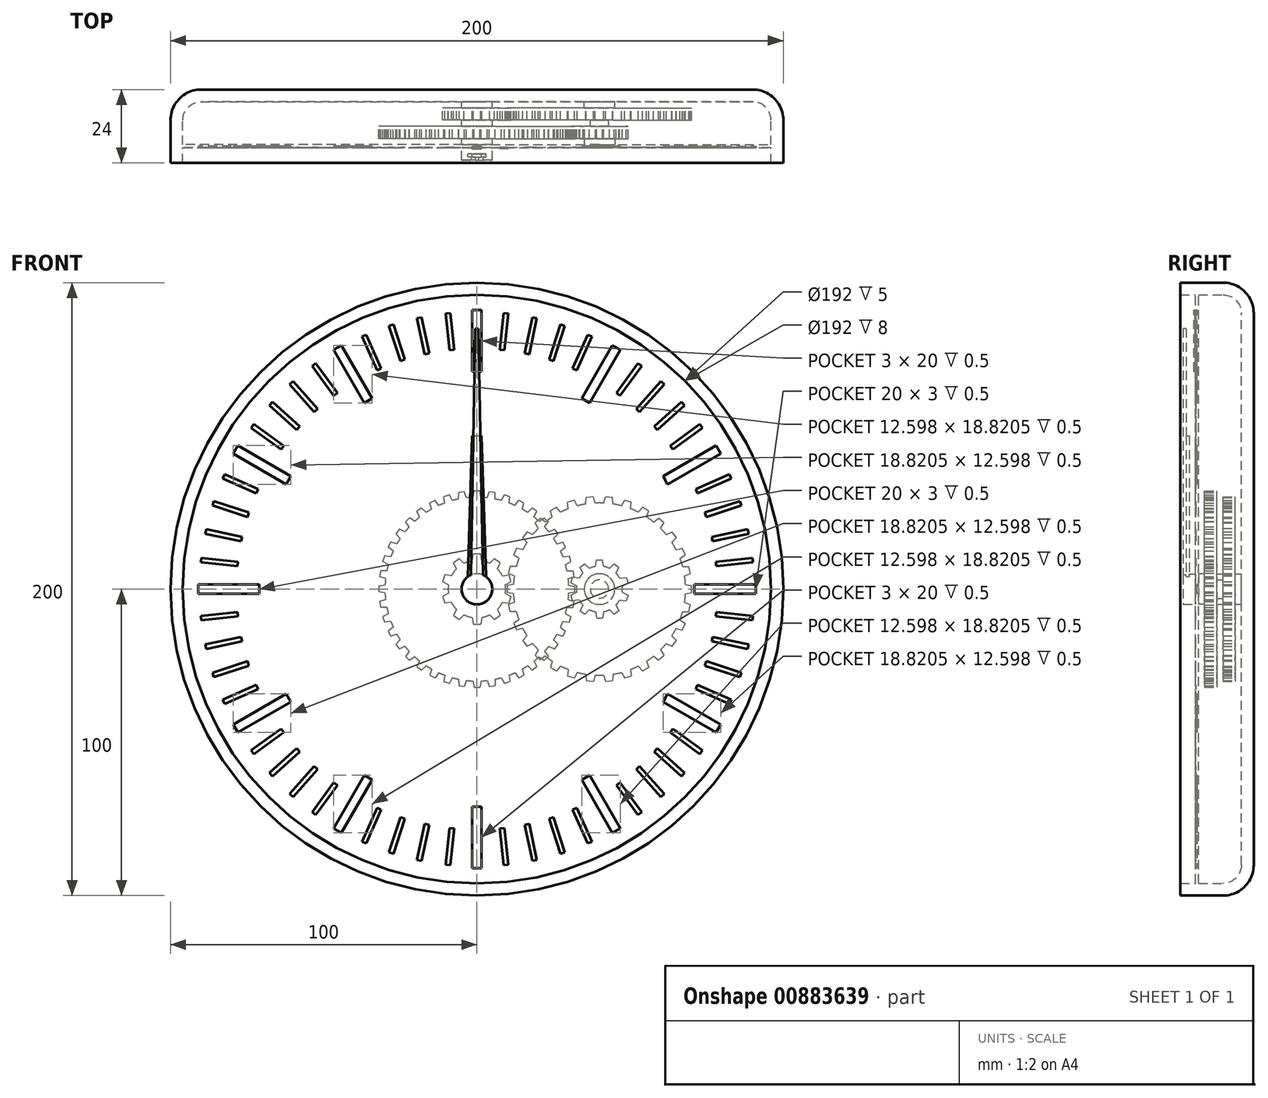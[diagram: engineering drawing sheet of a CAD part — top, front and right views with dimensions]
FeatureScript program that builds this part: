
annotation { "Feature Type Name" : "Feature", "Feature Type Description" : "" }
export const myFeature = defineFeature(function(context is Context, id is Id, definition is map)
    precondition{}
    {
        {
            var Q0;
            Q0=qCreatedBy(makeId("Front.planeOp"),FACE);
            var sketch = newSketch(context, id + "F0", { "sketchPlane" : qUnion([Q0])});
            skCircle(sketch, "E0", {"center": v(0, 0) * mm, "radius": 100 * mm});
            skSolve(sketch);
        }
        {
            var Q0;
            Q0 = qSketchRegion(id + "F0", true);
            extrude(context, id + "F1", {"entities" : qUnion([Q0]), "depth" : 24 * mm, "offsetDistance" : 25 * mm});
        }
        {
            var Q0;
            Q0=makeQuery(id+"F1.opExtrude","CAP_EDGE",EDGE,{"disambiguationData":[OSD([sQuery(id+"F0.wireOp",EDGE,"E0")])],"isStart":true});
            fillet(context, id + "F2", {"entities" : qUnion([Q0]), "radius" : 10 * mm, "tangentPropagation" : true, "allowEdgeOverflow" : false});
        }
        {
            var Q0;
            Q0=makeQuery(id+"F1.opExtrude","CAP_FACE",FACE,{"disambiguationData":[OSD([sQuery(id+"F0.wireOp",EDGE,"E0")])],"isStart":false});
            shell(context, id + "F3", {"entities" : qUnion([Q0]), "thickness" : 4 * mm});
        }
        {
            var Q0;
            {var subQ0=sQuery(id+"F0.wireOp",EDGE,"E0");Q0=makeQuery(id+"F3.opShell","OFFSET_FACE",FACE,{"disambiguationData":[OSD([subQ0]),TDD([makeQuery(id+"F1.opExtrude","CAP_FACE",FACE,{"disambiguationData":[OSD([subQ0])],"isStart":true})])]});}
            var sketch = newSketch(context, id + "F4", { "sketchPlane" : qUnion([Q0])});
            skCircle(sketch, "E1", {"center": v(0, 0) * mm, "radius": 5 * mm});
            skCircle(sketch, "E2", {"center": v(0, 0) * mm, "radius": 3 * mm});
            skCircle(sketch, "E3", {"center": v(40, 0) * mm, "radius": 5 * mm});
            skCircle(sketch, "E4", {"center": v(40, 0) * mm, "radius": 3 * mm});
            skSolve(sketch);
        }
        {
            var Q0;
            Q0 = qSketchRegion(id + "F4", true);
            extrude(context, id + "F5", {"entities" : qUnion([Q0]), "operationType" : NewBodyOperationType.ADD, "depth" : 2 * mm, "offsetDistance" : 25 * mm});
        }
        {
            var Q0;
            {var subQ0=sQuery(id+"F0.wireOp",EDGE,"E0");Q0=makeQuery(id+"F5.boolean.opBoolean","SPLIT",FACE,{"disambiguationData":[TD([makeQuery(id+"F5.opExtrude","SWEPT_FACE",FACE,{"disambiguationData":[OSD([sQuery(id+"F4.wireOp",EDGE,"E2")])]})])],"derivedFrom":makeQuery(id+"F3.opShell","OFFSET_FACE",FACE,{"disambiguationData":[OSD([subQ0]),TDD([makeQuery(id+"F1.opExtrude","CAP_FACE",FACE,{"disambiguationData":[OSD([subQ0])],"isStart":true})])]})});}
            extrude(context, id + "F6", {"entities" : qUnion([Q0]), "depth" : 19 * mm, "offsetDistance" : 25 * mm});
        }
        {
            var Q0;
            {var subQ0=sQuery(id+"F0.wireOp",EDGE,"E0");Q0=makeQuery(id+"F5.boolean.opBoolean","SPLIT",FACE,{"disambiguationData":[TD([makeQuery(id+"F5.opExtrude","SWEPT_FACE",FACE,{"disambiguationData":[OSD([sQuery(id+"F4.wireOp",EDGE,"E4")])]})])],"derivedFrom":makeQuery(id+"F3.opShell","OFFSET_FACE",FACE,{"disambiguationData":[OSD([subQ0]),TDD([makeQuery(id+"F1.opExtrude","CAP_FACE",FACE,{"disambiguationData":[OSD([subQ0])],"isStart":true})])]})});}
            extrude(context, id + "F7", {"entities" : qUnion([Q0]), "depth" : 8 * mm, "offsetDistance" : 25 * mm});
        }
        {
            var Q0;
            Q0=makeQuery(id+"F5.opExtrude","CAP_FACE",FACE,{"disambiguationData":[OSD([sQuery(id+"F4.wireOp",EDGE,"E1"),sQuery(id+"F4.wireOp",EDGE,"E2")])],"isStart":false});
            var sketch = newSketch(context, id + "F8", { "sketchPlane" : qUnion([Q0])});
            skCircle(sketch, "E5", {"center": v(0, 0) * mm, "radius": 9.38 * mm});
            skLineSegment(sketch, "E6", {"start": v(1.55, 9.25) * mm, "end": v(1.18, 11.38) * mm});
            skLineSegment(sketch, "E7", {"start": v(1.18, 11.38) * mm, "end": v(0, 11.38) * mm});
            skLineSegment(sketch, "E8.MirrorCS", {"start": v(-1.18, 11.38) * mm, "end": v(0, 11.38) * mm});
            skLineSegment(sketch, "E9.MirrorCS", {"start": v(-1.55, 9.25) * mm, "end": v(-1.18, 11.38) * mm});
            skLineSegment(sketch, "E10.1.0", {"start": v(-6.7, 6.57) * mm, "end": v(-7.64, 8.51) * mm});
            skLineSegment(sketch, "E10.1.1", {"start": v(-7.64, 8.51) * mm, "end": v(-6.69, 9.2) * mm});
            skLineSegment(sketch, "E10.1.2", {"start": v(-5.73, 9.9) * mm, "end": v(-6.69, 9.2) * mm});
            skLineSegment(sketch, "E10.1.3", {"start": v(-4.18, 8.4) * mm, "end": v(-5.73, 9.9) * mm});
            skLineSegment(sketch, "E10.2.0", {"start": v(-9.27, 1.38) * mm, "end": v(-11.18, 2.4) * mm});
            skLineSegment(sketch, "E10.2.1", {"start": v(-11.18, 2.4) * mm, "end": v(-10.82, 3.52) * mm});
            skLineSegment(sketch, "E10.2.2", {"start": v(-10.45, 4.64) * mm, "end": v(-10.82, 3.52) * mm});
            skLineSegment(sketch, "E10.2.3", {"start": v(-8.31, 4.33) * mm, "end": v(-10.45, 4.64) * mm});
            skLineSegment(sketch, "E11.1.3.0", {"start": v(-8.31, -4.33) * mm, "end": v(-10.45, -4.64) * mm});
            skLineSegment(sketch, "E11.3.3.0", {"start": v(-10.45, -4.64) * mm, "end": v(-10.82, -3.52) * mm});
            skLineSegment(sketch, "E11.6.3.0", {"start": v(-11.18, -2.4) * mm, "end": v(-10.82, -3.52) * mm});
            skLineSegment(sketch, "E11.9.3.0", {"start": v(-9.27, -1.38) * mm, "end": v(-11.18, -2.4) * mm});
            skLineSegment(sketch, "E11.1.4.0", {"start": v(-4.18, -8.4) * mm, "end": v(-5.73, -9.9) * mm});
            skLineSegment(sketch, "E11.3.4.0", {"start": v(-5.73, -9.9) * mm, "end": v(-6.69, -9.2) * mm});
            skLineSegment(sketch, "E11.6.4.0", {"start": v(-7.64, -8.51) * mm, "end": v(-6.69, -9.2) * mm});
            skLineSegment(sketch, "E11.9.4.0", {"start": v(-6.7, -6.57) * mm, "end": v(-7.64, -8.51) * mm});
            skLineSegment(sketch, "E11.1.5.0", {"start": v(1.55, -9.25) * mm, "end": v(1.18, -11.38) * mm});
            skLineSegment(sketch, "E11.3.5.0", {"start": v(1.18, -11.38) * mm, "end": v(0, -11.38) * mm});
            skLineSegment(sketch, "E11.6.5.0", {"start": v(-1.18, -11.38) * mm, "end": v(0, -11.38) * mm});
            skLineSegment(sketch, "E11.9.5.0", {"start": v(-1.55, -9.25) * mm, "end": v(-1.18, -11.38) * mm});
            skLineSegment(sketch, "E11.1.6.0", {"start": v(6.7, -6.57) * mm, "end": v(7.64, -8.51) * mm});
            skLineSegment(sketch, "E11.3.6.0", {"start": v(7.64, -8.51) * mm, "end": v(6.69, -9.2) * mm});
            skLineSegment(sketch, "E11.6.6.0", {"start": v(5.73, -9.9) * mm, "end": v(6.69, -9.2) * mm});
            skLineSegment(sketch, "E11.9.6.0", {"start": v(4.18, -8.4) * mm, "end": v(5.73, -9.9) * mm});
            skLineSegment(sketch, "E11.1.7.0", {"start": v(9.27, -1.38) * mm, "end": v(11.18, -2.4) * mm});
            skLineSegment(sketch, "E11.3.7.0", {"start": v(11.18, -2.4) * mm, "end": v(10.82, -3.52) * mm});
            skLineSegment(sketch, "E11.6.7.0", {"start": v(10.45, -4.64) * mm, "end": v(10.82, -3.52) * mm});
            skLineSegment(sketch, "E11.9.7.0", {"start": v(8.31, -4.33) * mm, "end": v(10.45, -4.64) * mm});
            skLineSegment(sketch, "E11.1.8.0", {"start": v(8.31, 4.33) * mm, "end": v(10.45, 4.64) * mm});
            skLineSegment(sketch, "E11.3.8.0", {"start": v(10.45, 4.64) * mm, "end": v(10.82, 3.52) * mm});
            skLineSegment(sketch, "E11.6.8.0", {"start": v(11.18, 2.4) * mm, "end": v(10.82, 3.52) * mm});
            skLineSegment(sketch, "E11.9.8.0", {"start": v(9.27, 1.38) * mm, "end": v(11.18, 2.4) * mm});
            skLineSegment(sketch, "E11.1.9.0", {"start": v(4.18, 8.4) * mm, "end": v(5.73, 9.9) * mm});
            skLineSegment(sketch, "E11.3.9.0", {"start": v(5.73, 9.9) * mm, "end": v(6.69, 9.2) * mm});
            skLineSegment(sketch, "E11.6.9.0", {"start": v(7.64, 8.51) * mm, "end": v(6.69, 9.2) * mm});
            skLineSegment(sketch, "E11.9.9.0", {"start": v(6.7, 6.57) * mm, "end": v(7.64, 8.51) * mm});
            skSolve(sketch);
        }
        {
            var Q0;
            Q0 = qSketchRegion(id + "F8", true);
            extrude(context, id + "F9", {"entities" : qUnion([Q0]), "operationType" : NewBodyOperationType.ADD, "depth" : 4 * mm, "offsetDistance" : 25 * mm});
        }
        {
            var Q0;
            Q0=makeQuery(id+"F5.opExtrude","CAP_FACE",FACE,{"disambiguationData":[OSD([sQuery(id+"F4.wireOp",EDGE,"E3"),sQuery(id+"F4.wireOp",EDGE,"E4")])],"isStart":false});
            var sketch = newSketch(context, id + "F10", { "sketchPlane" : qUnion([Q0])});
            skCircle(sketch, "E12", {"center": v(40, 0) * mm, "radius": 28.12 * mm});
            skLineSegment(sketch, "E13", {"start": v(11.92, 1.54) * mm, "end": v(9.88, 1.18) * mm});
            skLineSegment(sketch, "E14", {"start": v(9.88, 1.18) * mm, "end": v(9.88, 0) * mm});
            skLineSegment(sketch, "E15.MirrorCS", {"start": v(11.92, -1.54) * mm, "end": v(9.87, -1.18) * mm});
            skLineSegment(sketch, "E16.MirrorCS", {"start": v(9.88, -1.18) * mm, "end": v(9.88, 0) * mm});
            skLineSegment(sketch, "E17.1.0", {"start": v(12.21, -4.33) * mm, "end": v(10.29, -5.11) * mm});
            skLineSegment(sketch, "E17.1.1", {"start": v(10.29, -5.11) * mm, "end": v(10.53, -6.26) * mm});
            skLineSegment(sketch, "E17.1.2", {"start": v(10.78, -7.42) * mm, "end": v(10.53, -6.26) * mm});
            skLineSegment(sketch, "E17.1.3", {"start": v(12.85, -7.34) * mm, "end": v(10.78, -7.42) * mm});
            skLineSegment(sketch, "E17.2.0", {"start": v(13.72, -10.02) * mm, "end": v(12, -11.18) * mm});
            skLineSegment(sketch, "E17.2.1", {"start": v(12, -11.18) * mm, "end": v(12.48, -12.25) * mm});
            skLineSegment(sketch, "E17.2.2", {"start": v(12.96, -13.33) * mm, "end": v(12.48, -12.25) * mm});
            skLineSegment(sketch, "E17.2.3", {"start": v(14.97, -12.83) * mm, "end": v(12.96, -13.33) * mm});
            skLineSegment(sketch, "E18.2.3.0", {"start": v(16.38, -15.26) * mm, "end": v(14.94, -16.75) * mm});
            skLineSegment(sketch, "E18.3.3.0", {"start": v(14.94, -16.75) * mm, "end": v(15.63, -17.7) * mm});
            skLineSegment(sketch, "E18.6.3.0", {"start": v(16.32, -18.66) * mm, "end": v(15.63, -17.7) * mm});
            skLineSegment(sketch, "E18.9.3.0", {"start": v(18.18, -17.75) * mm, "end": v(16.32, -18.66) * mm});
            skLineSegment(sketch, "E18.2.4.0", {"start": v(20.07, -19.84) * mm, "end": v(18.97, -21.6) * mm});
            skLineSegment(sketch, "E18.3.4.0", {"start": v(18.97, -21.6) * mm, "end": v(19.84, -22.39) * mm});
            skLineSegment(sketch, "E18.6.4.0", {"start": v(20.72, -23.18) * mm, "end": v(19.84, -22.39) * mm});
            skLineSegment(sketch, "E18.9.4.0", {"start": v(22.35, -21.9) * mm, "end": v(20.72, -23.18) * mm});
            skLineSegment(sketch, "E18.2.5.0", {"start": v(24.63, -23.55) * mm, "end": v(23.92, -25.5) * mm});
            skLineSegment(sketch, "E18.3.5.0", {"start": v(23.92, -25.5) * mm, "end": v(24.94, -26.09) * mm});
            skLineSegment(sketch, "E18.6.5.0", {"start": v(25.96, -26.68) * mm, "end": v(24.94, -26.09) * mm});
            skLineSegment(sketch, "E18.9.5.0", {"start": v(27.3, -25.09) * mm, "end": v(25.96, -26.68) * mm});
            skLineSegment(sketch, "E18.2.6.0", {"start": v(29.86, -26.23) * mm, "end": v(29.57, -28.29) * mm});
            skLineSegment(sketch, "E18.3.6.0", {"start": v(29.57, -28.29) * mm, "end": v(30.7, -28.65) * mm});
            skLineSegment(sketch, "E18.6.6.0", {"start": v(31.81, -29.01) * mm, "end": v(30.7, -28.65) * mm});
            skLineSegment(sketch, "E18.9.6.0", {"start": v(32.78, -27.18) * mm, "end": v(31.81, -29.01) * mm});
            skLineSegment(sketch, "E18.2.7.0", {"start": v(35.53, -27.77) * mm, "end": v(35.68, -29.84) * mm});
            skLineSegment(sketch, "E18.3.7.0", {"start": v(35.68, -29.84) * mm, "end": v(36.85, -29.96) * mm});
            skLineSegment(sketch, "E18.6.7.0", {"start": v(38.02, -30.08) * mm, "end": v(36.85, -29.96) * mm});
            skLineSegment(sketch, "E18.9.7.0", {"start": v(38.6, -28.09) * mm, "end": v(38.02, -30.08) * mm});
            skLineSegment(sketch, "E18.2.8.0", {"start": v(41.4, -28.09) * mm, "end": v(41.98, -30.08) * mm});
            skLineSegment(sketch, "E18.3.8.0", {"start": v(41.98, -30.08) * mm, "end": v(43.15, -29.96) * mm});
            skLineSegment(sketch, "E18.6.8.0", {"start": v(44.32, -29.84) * mm, "end": v(43.15, -29.96) * mm});
            skLineSegment(sketch, "E18.9.8.0", {"start": v(44.47, -27.77) * mm, "end": v(44.32, -29.84) * mm});
            skLineSegment(sketch, "E18.2.9.0", {"start": v(47.22, -27.18) * mm, "end": v(48.19, -29.01) * mm});
            skLineSegment(sketch, "E18.3.9.0", {"start": v(48.19, -29.01) * mm, "end": v(49.3, -28.65) * mm});
            skLineSegment(sketch, "E18.6.9.0", {"start": v(50.43, -28.29) * mm, "end": v(49.3, -28.65) * mm});
            skLineSegment(sketch, "E18.9.9.0", {"start": v(50.14, -26.23) * mm, "end": v(50.43, -28.29) * mm});
            skLineSegment(sketch, "E18.2.10.0", {"start": v(52.7, -25.09) * mm, "end": v(54.04, -26.68) * mm});
            skLineSegment(sketch, "E18.3.10.0", {"start": v(54.04, -26.68) * mm, "end": v(55.06, -26.09) * mm});
            skLineSegment(sketch, "E18.6.10.0", {"start": v(56.08, -25.5) * mm, "end": v(55.06, -26.09) * mm});
            skLineSegment(sketch, "E18.9.10.0", {"start": v(55.37, -23.55) * mm, "end": v(56.08, -25.5) * mm});
            skLineSegment(sketch, "E18.2.11.0", {"start": v(57.65, -21.9) * mm, "end": v(59.28, -23.18) * mm});
            skLineSegment(sketch, "E18.3.11.0", {"start": v(59.28, -23.18) * mm, "end": v(60.16, -22.39) * mm});
            skLineSegment(sketch, "E18.6.11.0", {"start": v(61.03, -21.6) * mm, "end": v(60.16, -22.39) * mm});
            skLineSegment(sketch, "E18.9.11.0", {"start": v(59.93, -19.84) * mm, "end": v(61.03, -21.6) * mm});
            skLineSegment(sketch, "E18.2.12.0", {"start": v(61.82, -17.75) * mm, "end": v(63.68, -18.66) * mm});
            skLineSegment(sketch, "E18.3.12.0", {"start": v(63.68, -18.66) * mm, "end": v(64.37, -17.7) * mm});
            skLineSegment(sketch, "E18.6.12.0", {"start": v(65.06, -16.75) * mm, "end": v(64.37, -17.7) * mm});
            skLineSegment(sketch, "E18.9.12.0", {"start": v(63.62, -15.26) * mm, "end": v(65.06, -16.75) * mm});
            skLineSegment(sketch, "E18.2.13.0", {"start": v(65.03, -12.83) * mm, "end": v(67.04, -13.33) * mm});
            skLineSegment(sketch, "E18.3.13.0", {"start": v(67.04, -13.33) * mm, "end": v(67.52, -12.25) * mm});
            skLineSegment(sketch, "E18.6.13.0", {"start": v(68, -11.18) * mm, "end": v(67.52, -12.25) * mm});
            skLineSegment(sketch, "E18.9.13.0", {"start": v(66.28, -10.02) * mm, "end": v(68, -11.18) * mm});
            skLineSegment(sketch, "E18.2.14.0", {"start": v(67.15, -7.34) * mm, "end": v(69.22, -7.42) * mm});
            skLineSegment(sketch, "E18.3.14.0", {"start": v(69.22, -7.42) * mm, "end": v(69.47, -6.26) * mm});
            skLineSegment(sketch, "E18.6.14.0", {"start": v(69.71, -5.11) * mm, "end": v(69.47, -6.26) * mm});
            skLineSegment(sketch, "E18.9.14.0", {"start": v(67.79, -4.33) * mm, "end": v(69.71, -5.11) * mm});
            skLineSegment(sketch, "E18.2.15.0", {"start": v(68.08, -1.54) * mm, "end": v(70.12, -1.18) * mm});
            skLineSegment(sketch, "E18.3.15.0", {"start": v(70.12, -1.18) * mm, "end": v(70.12, 0) * mm});
            skLineSegment(sketch, "E18.6.15.0", {"start": v(70.12, 1.18) * mm, "end": v(70.12, 0) * mm});
            skLineSegment(sketch, "E18.9.15.0", {"start": v(68.08, 1.54) * mm, "end": v(70.13, 1.18) * mm});
            skLineSegment(sketch, "E18.2.16.0", {"start": v(67.79, 4.33) * mm, "end": v(69.71, 5.11) * mm});
            skLineSegment(sketch, "E18.3.16.0", {"start": v(69.71, 5.11) * mm, "end": v(69.47, 6.26) * mm});
            skLineSegment(sketch, "E18.6.16.0", {"start": v(69.22, 7.42) * mm, "end": v(69.47, 6.26) * mm});
            skLineSegment(sketch, "E18.9.16.0", {"start": v(67.15, 7.34) * mm, "end": v(69.22, 7.42) * mm});
            skLineSegment(sketch, "E18.2.17.0", {"start": v(66.28, 10.02) * mm, "end": v(68, 11.18) * mm});
            skLineSegment(sketch, "E18.3.17.0", {"start": v(68, 11.18) * mm, "end": v(67.52, 12.25) * mm});
            skLineSegment(sketch, "E18.6.17.0", {"start": v(67.04, 13.33) * mm, "end": v(67.52, 12.25) * mm});
            skLineSegment(sketch, "E18.9.17.0", {"start": v(65.03, 12.83) * mm, "end": v(67.04, 13.33) * mm});
            skLineSegment(sketch, "E18.2.18.0", {"start": v(63.62, 15.26) * mm, "end": v(65.06, 16.75) * mm});
            skLineSegment(sketch, "E18.3.18.0", {"start": v(65.06, 16.75) * mm, "end": v(64.37, 17.7) * mm});
            skLineSegment(sketch, "E18.6.18.0", {"start": v(63.68, 18.66) * mm, "end": v(64.37, 17.7) * mm});
            skLineSegment(sketch, "E18.9.18.0", {"start": v(61.82, 17.75) * mm, "end": v(63.68, 18.66) * mm});
            skLineSegment(sketch, "E18.2.19.0", {"start": v(59.93, 19.84) * mm, "end": v(61.03, 21.6) * mm});
            skLineSegment(sketch, "E18.3.19.0", {"start": v(61.03, 21.6) * mm, "end": v(60.16, 22.39) * mm});
            skLineSegment(sketch, "E18.6.19.0", {"start": v(59.28, 23.18) * mm, "end": v(60.16, 22.39) * mm});
            skLineSegment(sketch, "E18.9.19.0", {"start": v(57.65, 21.9) * mm, "end": v(59.28, 23.18) * mm});
            skLineSegment(sketch, "E18.2.20.0", {"start": v(55.37, 23.55) * mm, "end": v(56.08, 25.5) * mm});
            skLineSegment(sketch, "E18.3.20.0", {"start": v(56.08, 25.5) * mm, "end": v(55.06, 26.09) * mm});
            skLineSegment(sketch, "E18.6.20.0", {"start": v(54.04, 26.68) * mm, "end": v(55.06, 26.09) * mm});
            skLineSegment(sketch, "E18.9.20.0", {"start": v(52.7, 25.09) * mm, "end": v(54.04, 26.68) * mm});
            skLineSegment(sketch, "E18.2.21.0", {"start": v(50.14, 26.23) * mm, "end": v(50.43, 28.29) * mm});
            skLineSegment(sketch, "E18.3.21.0", {"start": v(50.43, 28.29) * mm, "end": v(49.3, 28.65) * mm});
            skLineSegment(sketch, "E18.6.21.0", {"start": v(48.19, 29.01) * mm, "end": v(49.3, 28.65) * mm});
            skLineSegment(sketch, "E18.9.21.0", {"start": v(47.22, 27.18) * mm, "end": v(48.19, 29.01) * mm});
            skLineSegment(sketch, "E18.2.22.0", {"start": v(44.47, 27.77) * mm, "end": v(44.32, 29.84) * mm});
            skLineSegment(sketch, "E18.3.22.0", {"start": v(44.32, 29.84) * mm, "end": v(43.15, 29.96) * mm});
            skLineSegment(sketch, "E18.6.22.0", {"start": v(41.98, 30.08) * mm, "end": v(43.15, 29.96) * mm});
            skLineSegment(sketch, "E18.9.22.0", {"start": v(41.4, 28.09) * mm, "end": v(41.98, 30.08) * mm});
            skLineSegment(sketch, "E18.2.23.0", {"start": v(38.6, 28.09) * mm, "end": v(38.02, 30.08) * mm});
            skLineSegment(sketch, "E18.3.23.0", {"start": v(38.02, 30.08) * mm, "end": v(36.85, 29.96) * mm});
            skLineSegment(sketch, "E18.6.23.0", {"start": v(35.68, 29.84) * mm, "end": v(36.85, 29.96) * mm});
            skLineSegment(sketch, "E18.9.23.0", {"start": v(35.53, 27.77) * mm, "end": v(35.68, 29.84) * mm});
            skLineSegment(sketch, "E18.2.24.0", {"start": v(32.78, 27.18) * mm, "end": v(31.81, 29.01) * mm});
            skLineSegment(sketch, "E18.3.24.0", {"start": v(31.81, 29.01) * mm, "end": v(30.7, 28.65) * mm});
            skLineSegment(sketch, "E18.6.24.0", {"start": v(29.57, 28.29) * mm, "end": v(30.7, 28.65) * mm});
            skLineSegment(sketch, "E18.9.24.0", {"start": v(29.86, 26.23) * mm, "end": v(29.57, 28.29) * mm});
            skLineSegment(sketch, "E18.2.25.0", {"start": v(27.3, 25.09) * mm, "end": v(25.96, 26.68) * mm});
            skLineSegment(sketch, "E18.3.25.0", {"start": v(25.96, 26.68) * mm, "end": v(24.94, 26.09) * mm});
            skLineSegment(sketch, "E18.6.25.0", {"start": v(23.92, 25.5) * mm, "end": v(24.94, 26.09) * mm});
            skLineSegment(sketch, "E18.9.25.0", {"start": v(24.63, 23.55) * mm, "end": v(23.92, 25.5) * mm});
            skLineSegment(sketch, "E18.2.26.0", {"start": v(22.35, 21.9) * mm, "end": v(20.72, 23.18) * mm});
            skLineSegment(sketch, "E18.3.26.0", {"start": v(20.72, 23.18) * mm, "end": v(19.84, 22.39) * mm});
            skLineSegment(sketch, "E18.6.26.0", {"start": v(18.97, 21.6) * mm, "end": v(19.84, 22.39) * mm});
            skLineSegment(sketch, "E18.9.26.0", {"start": v(20.07, 19.84) * mm, "end": v(18.97, 21.6) * mm});
            skLineSegment(sketch, "E18.2.27.0", {"start": v(18.18, 17.75) * mm, "end": v(16.32, 18.66) * mm});
            skLineSegment(sketch, "E18.3.27.0", {"start": v(16.32, 18.66) * mm, "end": v(15.63, 17.7) * mm});
            skLineSegment(sketch, "E18.6.27.0", {"start": v(14.94, 16.75) * mm, "end": v(15.63, 17.7) * mm});
            skLineSegment(sketch, "E18.9.27.0", {"start": v(16.38, 15.26) * mm, "end": v(14.94, 16.75) * mm});
            skLineSegment(sketch, "E18.2.28.0", {"start": v(14.97, 12.83) * mm, "end": v(12.96, 13.33) * mm});
            skLineSegment(sketch, "E18.3.28.0", {"start": v(12.96, 13.33) * mm, "end": v(12.48, 12.25) * mm});
            skLineSegment(sketch, "E18.6.28.0", {"start": v(12, 11.18) * mm, "end": v(12.48, 12.25) * mm});
            skLineSegment(sketch, "E18.9.28.0", {"start": v(13.72, 10.02) * mm, "end": v(12, 11.18) * mm});
            skLineSegment(sketch, "E18.2.29.0", {"start": v(12.85, 7.34) * mm, "end": v(10.78, 7.42) * mm});
            skLineSegment(sketch, "E18.3.29.0", {"start": v(10.78, 7.42) * mm, "end": v(10.53, 6.26) * mm});
            skLineSegment(sketch, "E18.6.29.0", {"start": v(10.29, 5.11) * mm, "end": v(10.53, 6.26) * mm});
            skLineSegment(sketch, "E18.9.29.0", {"start": v(12.21, 4.33) * mm, "end": v(10.29, 5.11) * mm});
            skSolve(sketch);
        }
        {
            var Q0;
            Q0 = qSketchRegion(id + "F10", true);
            extrude(context, id + "F11", {"entities" : qUnion([Q0]), "operationType" : NewBodyOperationType.ADD, "depth" : 4 * mm, "offsetDistance" : 25 * mm});
        }
        {
            var Q0;
            Q0=makeQuery(id+"F9.opExtrude","CAP_FACE",FACE,{"disambiguationData":[OSD([sQuery(id+"F8.wireOp",EDGE,"E5"),sQuery(id+"F8.wireOp",EDGE,"E6"),sQuery(id+"F8.wireOp",EDGE,"E7"),sQuery(id+"F8.wireOp",EDGE,"E8.MirrorCS"),sQuery(id+"F8.wireOp",EDGE,"E9.MirrorCS"),sQuery(id+"F8.wireOp",EDGE,"E10.1.0"),sQuery(id+"F8.wireOp",EDGE,"E10.1.1"),sQuery(id+"F8.wireOp",EDGE,"E10.1.2"),sQuery(id+"F8.wireOp",EDGE,"E10.1.3"),sQuery(id+"F8.wireOp",EDGE,"E10.2.0"),sQuery(id+"F8.wireOp",EDGE,"E10.2.1"),sQuery(id+"F8.wireOp",EDGE,"E10.2.2"),sQuery(id+"F8.wireOp",EDGE,"E10.2.3"),sQuery(id+"F8.wireOp",EDGE,"E11.1.3.0"),sQuery(id+"F8.wireOp",EDGE,"E11.3.3.0"),sQuery(id+"F8.wireOp",EDGE,"E11.6.3.0"),sQuery(id+"F8.wireOp",EDGE,"E11.9.3.0"),sQuery(id+"F8.wireOp",EDGE,"E11.1.4.0"),sQuery(id+"F8.wireOp",EDGE,"E11.3.4.0"),sQuery(id+"F8.wireOp",EDGE,"E11.6.4.0"),sQuery(id+"F8.wireOp",EDGE,"E11.9.4.0"),sQuery(id+"F8.wireOp",EDGE,"E11.1.5.0"),sQuery(id+"F8.wireOp",EDGE,"E11.3.5.0"),sQuery(id+"F8.wireOp",EDGE,"E11.6.5.0"),sQuery(id+"F8.wireOp",EDGE,"E11.9.5.0"),sQuery(id+"F8.wireOp",EDGE,"E11.1.6.0"),sQuery(id+"F8.wireOp",EDGE,"E11.3.6.0"),sQuery(id+"F8.wireOp",EDGE,"E11.6.6.0"),sQuery(id+"F8.wireOp",EDGE,"E11.9.6.0"),sQuery(id+"F8.wireOp",EDGE,"E11.1.7.0"),sQuery(id+"F8.wireOp",EDGE,"E11.3.7.0"),sQuery(id+"F8.wireOp",EDGE,"E11.6.7.0"),sQuery(id+"F8.wireOp",EDGE,"E11.9.7.0"),sQuery(id+"F8.wireOp",EDGE,"E11.1.8.0"),sQuery(id+"F8.wireOp",EDGE,"E11.3.8.0"),sQuery(id+"F8.wireOp",EDGE,"E11.6.8.0"),sQuery(id+"F8.wireOp",EDGE,"E11.9.8.0"),sQuery(id+"F8.wireOp",EDGE,"E11.1.9.0"),sQuery(id+"F8.wireOp",EDGE,"E11.3.9.0"),sQuery(id+"F8.wireOp",EDGE,"E11.6.9.0"),sQuery(id+"F8.wireOp",EDGE,"E11.9.9.0")])],"isStart":false});
            var sketch = newSketch(context, id + "F12", { "sketchPlane" : qUnion([Q0])});
            skCircle(sketch, "E19.0", {"center": v(0, 0) * mm, "radius": 3 * mm});
            skCircle(sketch, "E20.0", {"center": v(0, 0) * mm, "radius": 5 * mm});
            skSolve(sketch);
        }
        {
            var Q0;
            Q0 = qSketchRegion(id + "F12", true);
            extrude(context, id + "F13", {"entities" : qUnion([Q0]), "depth" : 2 * mm, "offsetDistance" : 25 * mm});
        }
        {
            var Q0;
            Q0=makeQuery(id+"F13.opExtrude","CAP_FACE",FACE,{"disambiguationData":[OSD([sQuery(id+"F12.wireOp",EDGE,"E19.0"),sQuery(id+"F12.wireOp",EDGE,"E20.0")])],"isStart":false});
            var sketch = newSketch(context, id + "F14", { "sketchPlane" : qUnion([Q0])});
            skCircle(sketch, "E21.0", {"center": v(0, 0) * mm, "radius": 3 * mm});
            skCircle(sketch, "E22", {"center": v(0, 0) * mm, "radius": 30 * mm});
            skLineSegment(sketch, "E23", {"start": v(1.3, 29.97) * mm, "end": v(0.94, 32) * mm});
            skLineSegment(sketch, "E24", {"start": v(0.94, 32) * mm, "end": v(0, 32) * mm});
            skLineSegment(sketch, "E25.MirrorCS", {"start": v(-1.3, 29.97) * mm, "end": v(-0.94, 32) * mm});
            skLineSegment(sketch, "E26.MirrorCS", {"start": v(-0.94, 32) * mm, "end": v(0, 32) * mm});
            skLineSegment(sketch, "E27.1.0", {"start": v(-3.4, 29.8) * mm, "end": v(-4.08, 31.75) * mm});
            skLineSegment(sketch, "E27.1.1", {"start": v(-4.08, 31.75) * mm, "end": v(-5, 31.6) * mm});
            skLineSegment(sketch, "E27.1.2", {"start": v(-5.94, 31.46) * mm, "end": v(-5, 31.6) * mm});
            skLineSegment(sketch, "E27.1.3", {"start": v(-5.97, 29.4) * mm, "end": v(-5.94, 31.46) * mm});
            skLineSegment(sketch, "E27.2.0", {"start": v(-8.03, 28.9) * mm, "end": v(-9, 30.73) * mm});
            skLineSegment(sketch, "E27.2.1", {"start": v(-9, 30.73) * mm, "end": v(-9.89, 30.43) * mm});
            skLineSegment(sketch, "E27.2.2", {"start": v(-10.78, 30.14) * mm, "end": v(-9.89, 30.43) * mm});
            skLineSegment(sketch, "E27.2.3", {"start": v(-10.5, 28.1) * mm, "end": v(-10.78, 30.14) * mm});
            skLineSegment(sketch, "E28.1.3.0", {"start": v(-12.45, 27.3) * mm, "end": v(-13.69, 28.94) * mm});
            skLineSegment(sketch, "E28.3.3.0", {"start": v(-13.69, 28.94) * mm, "end": v(-14.53, 28.51) * mm});
            skLineSegment(sketch, "E28.6.3.0", {"start": v(-15.37, 28.08) * mm, "end": v(-14.53, 28.51) * mm});
            skLineSegment(sketch, "E28.9.3.0", {"start": v(-14.77, 26.11) * mm, "end": v(-15.37, 28.08) * mm});
            skLineSegment(sketch, "E28.1.4.0", {"start": v(-16.57, 25.01) * mm, "end": v(-18.05, 26.44) * mm});
            skLineSegment(sketch, "E28.3.4.0", {"start": v(-18.05, 26.44) * mm, "end": v(-18.8, 25.89) * mm});
            skLineSegment(sketch, "E28.6.4.0", {"start": v(-19.57, 25.33) * mm, "end": v(-18.8, 25.89) * mm});
            skLineSegment(sketch, "E28.9.4.0", {"start": v(-18.67, 23.48) * mm, "end": v(-19.57, 25.33) * mm});
            skLineSegment(sketch, "E28.1.5.0", {"start": v(-20.27, 22.11) * mm, "end": v(-21.96, 23.3) * mm});
            skLineSegment(sketch, "E28.3.5.0", {"start": v(-21.96, 23.3) * mm, "end": v(-22.63, 22.63) * mm});
            skLineSegment(sketch, "E28.6.5.0", {"start": v(-23.3, 21.96) * mm, "end": v(-22.63, 22.63) * mm});
            skLineSegment(sketch, "E28.9.5.0", {"start": v(-22.11, 20.27) * mm, "end": v(-23.3, 21.96) * mm});
            skLineSegment(sketch, "E28.1.6.0", {"start": v(-23.48, 18.67) * mm, "end": v(-25.33, 19.57) * mm});
            skLineSegment(sketch, "E28.3.6.0", {"start": v(-25.33, 19.57) * mm, "end": v(-25.89, 18.8) * mm});
            skLineSegment(sketch, "E28.6.6.0", {"start": v(-26.44, 18.05) * mm, "end": v(-25.89, 18.8) * mm});
            skLineSegment(sketch, "E28.9.6.0", {"start": v(-25.01, 16.57) * mm, "end": v(-26.44, 18.05) * mm});
            skLineSegment(sketch, "E28.1.7.0", {"start": v(-26.11, 14.77) * mm, "end": v(-28.08, 15.37) * mm});
            skLineSegment(sketch, "E28.3.7.0", {"start": v(-28.08, 15.37) * mm, "end": v(-28.51, 14.53) * mm});
            skLineSegment(sketch, "E28.6.7.0", {"start": v(-28.94, 13.69) * mm, "end": v(-28.51, 14.53) * mm});
            skLineSegment(sketch, "E28.9.7.0", {"start": v(-27.3, 12.45) * mm, "end": v(-28.94, 13.69) * mm});
            skLineSegment(sketch, "E28.1.8.0", {"start": v(-28.1, 10.5) * mm, "end": v(-30.14, 10.78) * mm});
            skLineSegment(sketch, "E28.3.8.0", {"start": v(-30.14, 10.78) * mm, "end": v(-30.43, 9.89) * mm});
            skLineSegment(sketch, "E28.6.8.0", {"start": v(-30.73, 9) * mm, "end": v(-30.43, 9.89) * mm});
            skLineSegment(sketch, "E28.9.8.0", {"start": v(-28.9, 8.03) * mm, "end": v(-30.73, 9) * mm});
            skLineSegment(sketch, "E28.1.9.0", {"start": v(-29.4, 5.97) * mm, "end": v(-31.46, 5.94) * mm});
            skLineSegment(sketch, "E28.3.9.0", {"start": v(-31.46, 5.94) * mm, "end": v(-31.6, 5) * mm});
            skLineSegment(sketch, "E28.6.9.0", {"start": v(-31.75, 4.08) * mm, "end": v(-31.6, 5) * mm});
            skLineSegment(sketch, "E28.9.9.0", {"start": v(-29.8, 3.4) * mm, "end": v(-31.75, 4.08) * mm});
            skLineSegment(sketch, "E28.1.10.0", {"start": v(-29.97, 1.3) * mm, "end": v(-32, 0.94) * mm});
            skLineSegment(sketch, "E28.3.10.0", {"start": v(-32, 0.94) * mm, "end": v(-32, 0) * mm});
            skLineSegment(sketch, "E28.6.10.0", {"start": v(-32, -0.94) * mm, "end": v(-32, 0) * mm});
            skLineSegment(sketch, "E28.9.10.0", {"start": v(-29.97, -1.3) * mm, "end": v(-32, -0.94) * mm});
            skLineSegment(sketch, "E28.1.11.0", {"start": v(-29.8, -3.4) * mm, "end": v(-31.75, -4.08) * mm});
            skLineSegment(sketch, "E28.3.11.0", {"start": v(-31.75, -4.08) * mm, "end": v(-31.6, -5) * mm});
            skLineSegment(sketch, "E28.6.11.0", {"start": v(-31.46, -5.94) * mm, "end": v(-31.6, -5) * mm});
            skLineSegment(sketch, "E28.9.11.0", {"start": v(-29.4, -5.97) * mm, "end": v(-31.46, -5.94) * mm});
            skLineSegment(sketch, "E28.1.12.0", {"start": v(-28.9, -8.03) * mm, "end": v(-30.73, -9) * mm});
            skLineSegment(sketch, "E28.3.12.0", {"start": v(-30.73, -9) * mm, "end": v(-30.43, -9.89) * mm});
            skLineSegment(sketch, "E28.6.12.0", {"start": v(-30.14, -10.78) * mm, "end": v(-30.43, -9.89) * mm});
            skLineSegment(sketch, "E28.9.12.0", {"start": v(-28.1, -10.5) * mm, "end": v(-30.14, -10.78) * mm});
            skLineSegment(sketch, "E28.1.13.0", {"start": v(-27.3, -12.45) * mm, "end": v(-28.94, -13.69) * mm});
            skLineSegment(sketch, "E28.3.13.0", {"start": v(-28.94, -13.69) * mm, "end": v(-28.51, -14.53) * mm});
            skLineSegment(sketch, "E28.6.13.0", {"start": v(-28.08, -15.37) * mm, "end": v(-28.51, -14.53) * mm});
            skLineSegment(sketch, "E28.9.13.0", {"start": v(-26.11, -14.77) * mm, "end": v(-28.08, -15.37) * mm});
            skLineSegment(sketch, "E28.1.14.0", {"start": v(-25.01, -16.57) * mm, "end": v(-26.44, -18.05) * mm});
            skLineSegment(sketch, "E28.3.14.0", {"start": v(-26.44, -18.05) * mm, "end": v(-25.89, -18.8) * mm});
            skLineSegment(sketch, "E28.6.14.0", {"start": v(-25.33, -19.57) * mm, "end": v(-25.89, -18.8) * mm});
            skLineSegment(sketch, "E28.9.14.0", {"start": v(-23.48, -18.67) * mm, "end": v(-25.33, -19.57) * mm});
            skLineSegment(sketch, "E28.1.15.0", {"start": v(-22.11, -20.27) * mm, "end": v(-23.3, -21.96) * mm});
            skLineSegment(sketch, "E28.3.15.0", {"start": v(-23.3, -21.96) * mm, "end": v(-22.63, -22.63) * mm});
            skLineSegment(sketch, "E28.6.15.0", {"start": v(-21.96, -23.3) * mm, "end": v(-22.63, -22.63) * mm});
            skLineSegment(sketch, "E28.9.15.0", {"start": v(-20.27, -22.11) * mm, "end": v(-21.96, -23.3) * mm});
            skLineSegment(sketch, "E28.1.16.0", {"start": v(-18.67, -23.48) * mm, "end": v(-19.57, -25.33) * mm});
            skLineSegment(sketch, "E28.3.16.0", {"start": v(-19.57, -25.33) * mm, "end": v(-18.8, -25.89) * mm});
            skLineSegment(sketch, "E28.6.16.0", {"start": v(-18.05, -26.44) * mm, "end": v(-18.8, -25.89) * mm});
            skLineSegment(sketch, "E28.9.16.0", {"start": v(-16.57, -25.01) * mm, "end": v(-18.05, -26.44) * mm});
            skLineSegment(sketch, "E28.1.17.0", {"start": v(-14.77, -26.11) * mm, "end": v(-15.37, -28.08) * mm});
            skLineSegment(sketch, "E28.3.17.0", {"start": v(-15.37, -28.08) * mm, "end": v(-14.53, -28.51) * mm});
            skLineSegment(sketch, "E28.6.17.0", {"start": v(-13.69, -28.94) * mm, "end": v(-14.53, -28.51) * mm});
            skLineSegment(sketch, "E28.9.17.0", {"start": v(-12.45, -27.3) * mm, "end": v(-13.69, -28.94) * mm});
            skLineSegment(sketch, "E28.1.18.0", {"start": v(-10.5, -28.1) * mm, "end": v(-10.78, -30.14) * mm});
            skLineSegment(sketch, "E28.3.18.0", {"start": v(-10.78, -30.14) * mm, "end": v(-9.89, -30.43) * mm});
            skLineSegment(sketch, "E28.6.18.0", {"start": v(-9, -30.73) * mm, "end": v(-9.89, -30.43) * mm});
            skLineSegment(sketch, "E28.9.18.0", {"start": v(-8.03, -28.9) * mm, "end": v(-9, -30.73) * mm});
            skLineSegment(sketch, "E28.1.19.0", {"start": v(-5.97, -29.4) * mm, "end": v(-5.94, -31.46) * mm});
            skLineSegment(sketch, "E28.3.19.0", {"start": v(-5.94, -31.46) * mm, "end": v(-5, -31.6) * mm});
            skLineSegment(sketch, "E28.6.19.0", {"start": v(-4.08, -31.75) * mm, "end": v(-5, -31.6) * mm});
            skLineSegment(sketch, "E28.9.19.0", {"start": v(-3.4, -29.8) * mm, "end": v(-4.08, -31.75) * mm});
            skLineSegment(sketch, "E28.1.20.0", {"start": v(-1.3, -29.97) * mm, "end": v(-0.94, -32) * mm});
            skLineSegment(sketch, "E28.3.20.0", {"start": v(-0.94, -32) * mm, "end": v(0, -32) * mm});
            skLineSegment(sketch, "E28.6.20.0", {"start": v(0.94, -32) * mm, "end": v(0, -32) * mm});
            skLineSegment(sketch, "E28.9.20.0", {"start": v(1.3, -29.97) * mm, "end": v(0.94, -32) * mm});
            skLineSegment(sketch, "E28.1.21.0", {"start": v(3.4, -29.8) * mm, "end": v(4.08, -31.75) * mm});
            skLineSegment(sketch, "E28.3.21.0", {"start": v(4.08, -31.75) * mm, "end": v(5, -31.6) * mm});
            skLineSegment(sketch, "E28.6.21.0", {"start": v(5.94, -31.46) * mm, "end": v(5, -31.6) * mm});
            skLineSegment(sketch, "E28.9.21.0", {"start": v(5.97, -29.4) * mm, "end": v(5.94, -31.46) * mm});
            skLineSegment(sketch, "E28.1.22.0", {"start": v(8.03, -28.9) * mm, "end": v(9, -30.73) * mm});
            skLineSegment(sketch, "E28.3.22.0", {"start": v(9, -30.73) * mm, "end": v(9.89, -30.43) * mm});
            skLineSegment(sketch, "E28.6.22.0", {"start": v(10.78, -30.14) * mm, "end": v(9.89, -30.43) * mm});
            skLineSegment(sketch, "E28.9.22.0", {"start": v(10.5, -28.1) * mm, "end": v(10.78, -30.14) * mm});
            skLineSegment(sketch, "E28.1.23.0", {"start": v(12.45, -27.3) * mm, "end": v(13.69, -28.94) * mm});
            skLineSegment(sketch, "E28.3.23.0", {"start": v(13.69, -28.94) * mm, "end": v(14.53, -28.51) * mm});
            skLineSegment(sketch, "E28.6.23.0", {"start": v(15.37, -28.08) * mm, "end": v(14.53, -28.51) * mm});
            skLineSegment(sketch, "E28.9.23.0", {"start": v(14.77, -26.11) * mm, "end": v(15.37, -28.08) * mm});
            skLineSegment(sketch, "E28.1.24.0", {"start": v(16.57, -25.01) * mm, "end": v(18.05, -26.44) * mm});
            skLineSegment(sketch, "E28.3.24.0", {"start": v(18.05, -26.44) * mm, "end": v(18.8, -25.89) * mm});
            skLineSegment(sketch, "E28.6.24.0", {"start": v(19.57, -25.33) * mm, "end": v(18.8, -25.89) * mm});
            skLineSegment(sketch, "E28.9.24.0", {"start": v(18.67, -23.48) * mm, "end": v(19.57, -25.33) * mm});
            skLineSegment(sketch, "E28.1.25.0", {"start": v(20.27, -22.11) * mm, "end": v(21.96, -23.3) * mm});
            skLineSegment(sketch, "E28.3.25.0", {"start": v(21.96, -23.3) * mm, "end": v(22.63, -22.63) * mm});
            skLineSegment(sketch, "E28.6.25.0", {"start": v(23.3, -21.96) * mm, "end": v(22.63, -22.63) * mm});
            skLineSegment(sketch, "E28.9.25.0", {"start": v(22.11, -20.27) * mm, "end": v(23.3, -21.96) * mm});
            skLineSegment(sketch, "E28.1.26.0", {"start": v(23.48, -18.67) * mm, "end": v(25.33, -19.57) * mm});
            skLineSegment(sketch, "E28.3.26.0", {"start": v(25.33, -19.57) * mm, "end": v(25.89, -18.8) * mm});
            skLineSegment(sketch, "E28.6.26.0", {"start": v(26.44, -18.05) * mm, "end": v(25.89, -18.8) * mm});
            skLineSegment(sketch, "E28.9.26.0", {"start": v(25.01, -16.57) * mm, "end": v(26.44, -18.05) * mm});
            skLineSegment(sketch, "E28.1.27.0", {"start": v(26.11, -14.77) * mm, "end": v(28.08, -15.37) * mm});
            skLineSegment(sketch, "E28.3.27.0", {"start": v(28.08, -15.37) * mm, "end": v(28.51, -14.53) * mm});
            skLineSegment(sketch, "E28.6.27.0", {"start": v(28.94, -13.69) * mm, "end": v(28.51, -14.53) * mm});
            skLineSegment(sketch, "E28.9.27.0", {"start": v(27.3, -12.45) * mm, "end": v(28.94, -13.69) * mm});
            skLineSegment(sketch, "E28.1.28.0", {"start": v(28.1, -10.5) * mm, "end": v(30.14, -10.78) * mm});
            skLineSegment(sketch, "E28.3.28.0", {"start": v(30.14, -10.78) * mm, "end": v(30.43, -9.89) * mm});
            skLineSegment(sketch, "E28.6.28.0", {"start": v(30.73, -9) * mm, "end": v(30.43, -9.89) * mm});
            skLineSegment(sketch, "E28.9.28.0", {"start": v(28.9, -8.03) * mm, "end": v(30.73, -9) * mm});
            skLineSegment(sketch, "E28.1.29.0", {"start": v(29.4, -5.97) * mm, "end": v(31.46, -5.94) * mm});
            skLineSegment(sketch, "E28.3.29.0", {"start": v(31.46, -5.94) * mm, "end": v(31.6, -5) * mm});
            skLineSegment(sketch, "E28.6.29.0", {"start": v(31.75, -4.08) * mm, "end": v(31.6, -5) * mm});
            skLineSegment(sketch, "E28.9.29.0", {"start": v(29.8, -3.4) * mm, "end": v(31.75, -4.08) * mm});
            skLineSegment(sketch, "E28.1.30.0", {"start": v(29.97, -1.3) * mm, "end": v(32, -0.94) * mm});
            skLineSegment(sketch, "E28.3.30.0", {"start": v(32, -0.94) * mm, "end": v(32, 0) * mm});
            skLineSegment(sketch, "E28.6.30.0", {"start": v(32, 0.94) * mm, "end": v(32, 0) * mm});
            skLineSegment(sketch, "E28.9.30.0", {"start": v(29.97, 1.3) * mm, "end": v(32, 0.94) * mm});
            skLineSegment(sketch, "E28.1.31.0", {"start": v(29.8, 3.4) * mm, "end": v(31.75, 4.08) * mm});
            skLineSegment(sketch, "E28.3.31.0", {"start": v(31.75, 4.08) * mm, "end": v(31.6, 5) * mm});
            skLineSegment(sketch, "E28.6.31.0", {"start": v(31.46, 5.94) * mm, "end": v(31.6, 5) * mm});
            skLineSegment(sketch, "E28.9.31.0", {"start": v(29.4, 5.97) * mm, "end": v(31.46, 5.94) * mm});
            skLineSegment(sketch, "E28.1.32.0", {"start": v(28.9, 8.03) * mm, "end": v(30.73, 9) * mm});
            skLineSegment(sketch, "E28.3.32.0", {"start": v(30.73, 9) * mm, "end": v(30.43, 9.89) * mm});
            skLineSegment(sketch, "E28.6.32.0", {"start": v(30.14, 10.78) * mm, "end": v(30.43, 9.89) * mm});
            skLineSegment(sketch, "E28.9.32.0", {"start": v(28.1, 10.5) * mm, "end": v(30.14, 10.78) * mm});
            skLineSegment(sketch, "E28.1.33.0", {"start": v(27.3, 12.45) * mm, "end": v(28.94, 13.69) * mm});
            skLineSegment(sketch, "E28.3.33.0", {"start": v(28.94, 13.69) * mm, "end": v(28.51, 14.53) * mm});
            skLineSegment(sketch, "E28.6.33.0", {"start": v(28.08, 15.37) * mm, "end": v(28.51, 14.53) * mm});
            skLineSegment(sketch, "E28.9.33.0", {"start": v(26.11, 14.77) * mm, "end": v(28.08, 15.37) * mm});
            skLineSegment(sketch, "E28.1.34.0", {"start": v(25.01, 16.57) * mm, "end": v(26.44, 18.05) * mm});
            skLineSegment(sketch, "E28.3.34.0", {"start": v(26.44, 18.05) * mm, "end": v(25.89, 18.8) * mm});
            skLineSegment(sketch, "E28.6.34.0", {"start": v(25.33, 19.57) * mm, "end": v(25.89, 18.8) * mm});
            skLineSegment(sketch, "E28.9.34.0", {"start": v(23.48, 18.67) * mm, "end": v(25.33, 19.57) * mm});
            skLineSegment(sketch, "E28.1.35.0", {"start": v(22.11, 20.27) * mm, "end": v(23.3, 21.96) * mm});
            skLineSegment(sketch, "E28.3.35.0", {"start": v(23.3, 21.96) * mm, "end": v(22.63, 22.63) * mm});
            skLineSegment(sketch, "E28.6.35.0", {"start": v(21.96, 23.3) * mm, "end": v(22.63, 22.63) * mm});
            skLineSegment(sketch, "E28.9.35.0", {"start": v(20.27, 22.11) * mm, "end": v(21.96, 23.3) * mm});
            skLineSegment(sketch, "E28.1.36.0", {"start": v(18.67, 23.48) * mm, "end": v(19.57, 25.33) * mm});
            skLineSegment(sketch, "E28.3.36.0", {"start": v(19.57, 25.33) * mm, "end": v(18.8, 25.89) * mm});
            skLineSegment(sketch, "E28.6.36.0", {"start": v(18.05, 26.44) * mm, "end": v(18.8, 25.89) * mm});
            skLineSegment(sketch, "E28.9.36.0", {"start": v(16.57, 25.01) * mm, "end": v(18.05, 26.44) * mm});
            skLineSegment(sketch, "E28.1.37.0", {"start": v(14.77, 26.11) * mm, "end": v(15.37, 28.08) * mm});
            skLineSegment(sketch, "E28.3.37.0", {"start": v(15.37, 28.08) * mm, "end": v(14.53, 28.51) * mm});
            skLineSegment(sketch, "E28.6.37.0", {"start": v(13.69, 28.94) * mm, "end": v(14.53, 28.51) * mm});
            skLineSegment(sketch, "E28.9.37.0", {"start": v(12.45, 27.3) * mm, "end": v(13.69, 28.94) * mm});
            skLineSegment(sketch, "E28.1.38.0", {"start": v(10.5, 28.1) * mm, "end": v(10.78, 30.14) * mm});
            skLineSegment(sketch, "E28.3.38.0", {"start": v(10.78, 30.14) * mm, "end": v(9.89, 30.43) * mm});
            skLineSegment(sketch, "E28.6.38.0", {"start": v(9, 30.73) * mm, "end": v(9.89, 30.43) * mm});
            skLineSegment(sketch, "E28.9.38.0", {"start": v(8.03, 28.9) * mm, "end": v(9, 30.73) * mm});
            skLineSegment(sketch, "E28.1.39.0", {"start": v(5.97, 29.4) * mm, "end": v(5.94, 31.46) * mm});
            skLineSegment(sketch, "E28.3.39.0", {"start": v(5.94, 31.46) * mm, "end": v(5, 31.6) * mm});
            skLineSegment(sketch, "E28.6.39.0", {"start": v(4.08, 31.75) * mm, "end": v(5, 31.6) * mm});
            skLineSegment(sketch, "E28.9.39.0", {"start": v(3.4, 29.8) * mm, "end": v(4.08, 31.75) * mm});
            skSolve(sketch);
        }
        {
            var Q0;
            Q0 = qSketchRegion(id + "F14", true);
            extrude(context, id + "F15", {"entities" : qUnion([Q0]), "operationType" : NewBodyOperationType.ADD, "depth" : 4 * mm, "offsetDistance" : 25 * mm});
        }
        {
            var Q0;
            Q0=makeQuery(id+"F7.opExtrude","CAP_FACE",FACE,{"disambiguationData":[OSD([sQuery(id+"F0.wireOp",EDGE,"E0")])],"isStart":false});
            var sketch = newSketch(context, id + "F16", { "sketchPlane" : qUnion([Q0])});
            skCircle(sketch, "E29", {"center": v(40, 0) * mm, "radius": 7.5 * mm});
            skLineSegment(sketch, "E30", {"start": v(40, 0) * mm, "end": v(40, 7.5) * mm, "construction": true});
            skLineSegment(sketch, "E31", {"start": v(38.68, 7.38) * mm, "end": v(39.06, 9.5) * mm});
            skLineSegment(sketch, "E32", {"start": v(39.06, 9.5) * mm, "end": v(40.94, 9.5) * mm});
            skLineSegment(sketch, "E33.MirrorCS", {"start": v(41.32, 7.38) * mm, "end": v(40.94, 9.5) * mm});
            skLineSegment(sketch, "E34.1.0", {"start": v(33.65, 7.13) * mm, "end": v(35.18, 8.24) * mm});
            skLineSegment(sketch, "E34.1.1", {"start": v(36.72, 6.75) * mm, "end": v(35.18, 8.24) * mm});
            skLineSegment(sketch, "E34.1.2", {"start": v(34.6, 5.2) * mm, "end": v(33.65, 7.13) * mm});
            skLineSegment(sketch, "E34.2.0", {"start": v(30.67, 2.04) * mm, "end": v(31.26, 3.83) * mm});
            skLineSegment(sketch, "E34.2.1", {"start": v(33.38, 3.53) * mm, "end": v(31.26, 3.83) * mm});
            skLineSegment(sketch, "E34.2.2", {"start": v(32.57, 1.03) * mm, "end": v(30.67, 2.04) * mm});
            skLineSegment(sketch, "E35.1.3.0", {"start": v(31.26, -3.83) * mm, "end": v(30.67, -2.04) * mm});
            skLineSegment(sketch, "E35.3.3.0", {"start": v(32.57, -1.03) * mm, "end": v(30.67, -2.04) * mm});
            skLineSegment(sketch, "E35.6.3.0", {"start": v(33.38, -3.53) * mm, "end": v(31.26, -3.83) * mm});
            skLineSegment(sketch, "E35.1.4.0", {"start": v(35.18, -8.24) * mm, "end": v(33.65, -7.13) * mm});
            skLineSegment(sketch, "E35.3.4.0", {"start": v(34.6, -5.2) * mm, "end": v(33.65, -7.13) * mm});
            skLineSegment(sketch, "E35.6.4.0", {"start": v(36.72, -6.75) * mm, "end": v(35.18, -8.24) * mm});
            skLineSegment(sketch, "E35.1.5.0", {"start": v(40.94, -9.5) * mm, "end": v(39.06, -9.5) * mm});
            skLineSegment(sketch, "E35.3.5.0", {"start": v(38.68, -7.38) * mm, "end": v(39.06, -9.5) * mm});
            skLineSegment(sketch, "E35.6.5.0", {"start": v(41.32, -7.38) * mm, "end": v(40.94, -9.5) * mm});
            skLineSegment(sketch, "E35.1.6.0", {"start": v(46.35, -7.13) * mm, "end": v(44.82, -8.24) * mm});
            skLineSegment(sketch, "E35.3.6.0", {"start": v(43.28, -6.75) * mm, "end": v(44.82, -8.24) * mm});
            skLineSegment(sketch, "E35.6.6.0", {"start": v(45.4, -5.2) * mm, "end": v(46.35, -7.13) * mm});
            skLineSegment(sketch, "E35.1.7.0", {"start": v(49.33, -2.04) * mm, "end": v(48.74, -3.83) * mm});
            skLineSegment(sketch, "E35.3.7.0", {"start": v(46.62, -3.53) * mm, "end": v(48.74, -3.83) * mm});
            skLineSegment(sketch, "E35.6.7.0", {"start": v(47.43, -1.03) * mm, "end": v(49.33, -2.04) * mm});
            skLineSegment(sketch, "E35.1.8.0", {"start": v(48.74, 3.83) * mm, "end": v(49.33, 2.04) * mm});
            skLineSegment(sketch, "E35.3.8.0", {"start": v(47.43, 1.03) * mm, "end": v(49.33, 2.04) * mm});
            skLineSegment(sketch, "E35.6.8.0", {"start": v(46.62, 3.53) * mm, "end": v(48.74, 3.83) * mm});
            skLineSegment(sketch, "E35.1.9.0", {"start": v(44.82, 8.24) * mm, "end": v(46.35, 7.13) * mm});
            skLineSegment(sketch, "E35.3.9.0", {"start": v(45.4, 5.2) * mm, "end": v(46.35, 7.13) * mm});
            skLineSegment(sketch, "E35.6.9.0", {"start": v(43.28, 6.75) * mm, "end": v(44.82, 8.24) * mm});
            skSolve(sketch);
        }
        {
            var Q0;
            Q0 = qSketchRegion(id + "F16", true);
            extrude(context, id + "F17", {"entities" : qUnion([Q0]), "operationType" : NewBodyOperationType.ADD, "depth" : 4 * mm, "offsetDistance" : 25 * mm});
        }
        {
            var Q0;
            Q0=makeQuery(id+"F17.opExtrude","CAP_FACE",FACE,{"disambiguationData":[OSD([sQuery(id+"F16.wireOp",EDGE,"E29"),sQuery(id+"F16.wireOp",EDGE,"E31"),sQuery(id+"F16.wireOp",EDGE,"E32"),sQuery(id+"F16.wireOp",EDGE,"E33.MirrorCS"),sQuery(id+"F16.wireOp",EDGE,"E34.1.0"),sQuery(id+"F16.wireOp",EDGE,"E34.1.1"),sQuery(id+"F16.wireOp",EDGE,"E34.1.2"),sQuery(id+"F16.wireOp",EDGE,"E34.2.0"),sQuery(id+"F16.wireOp",EDGE,"E34.2.1"),sQuery(id+"F16.wireOp",EDGE,"E34.2.2"),sQuery(id+"F16.wireOp",EDGE,"E35.1.3.0"),sQuery(id+"F16.wireOp",EDGE,"E35.3.3.0"),sQuery(id+"F16.wireOp",EDGE,"E35.6.3.0"),sQuery(id+"F16.wireOp",EDGE,"E35.1.4.0"),sQuery(id+"F16.wireOp",EDGE,"E35.3.4.0"),sQuery(id+"F16.wireOp",EDGE,"E35.6.4.0"),sQuery(id+"F16.wireOp",EDGE,"E35.1.5.0"),sQuery(id+"F16.wireOp",EDGE,"E35.3.5.0"),sQuery(id+"F16.wireOp",EDGE,"E35.6.5.0"),sQuery(id+"F16.wireOp",EDGE,"E35.1.6.0"),sQuery(id+"F16.wireOp",EDGE,"E35.3.6.0"),sQuery(id+"F16.wireOp",EDGE,"E35.6.6.0"),sQuery(id+"F16.wireOp",EDGE,"E35.1.7.0"),sQuery(id+"F16.wireOp",EDGE,"E35.3.7.0"),sQuery(id+"F16.wireOp",EDGE,"E35.6.7.0"),sQuery(id+"F16.wireOp",EDGE,"E35.1.8.0"),sQuery(id+"F16.wireOp",EDGE,"E35.3.8.0"),sQuery(id+"F16.wireOp",EDGE,"E35.6.8.0"),sQuery(id+"F16.wireOp",EDGE,"E35.1.9.0"),sQuery(id+"F16.wireOp",EDGE,"E35.3.9.0"),sQuery(id+"F16.wireOp",EDGE,"E35.6.9.0")])],"isStart":false});
            var sketch = newSketch(context, id + "F18", { "sketchPlane" : qUnion([Q0])});
            skCircle(sketch, "E36.0", {"center": v(40, 0) * mm, "radius": 3 * mm});
            skSolve(sketch);
        }
        {
            var Q0;
            Q0 = qSketchRegion(id + "F18", true);
            extrude(context, id + "F19", {"entities" : qUnion([Q0]), "operationType" : NewBodyOperationType.ADD, "depth" : 2 * mm, "offsetDistance" : 25 * mm});
        }
        {
            var Q0;
            Q0=makeQuery(id+"F19.opExtrude","CAP_FACE",FACE,{"disambiguationData":[OSD([sQuery(id+"F18.wireOp",EDGE,"E36.0")])],"isStart":false});
            var sketch = newSketch(context, id + "F20", { "sketchPlane" : qUnion([Q0])});
            skCircle(sketch, "E37", {"center": v(0, 0) * mm, "radius": 98 * mm});
            skCircle(sketch, "E38.0", {"center": v(0, 0) * mm, "radius": 5 * mm});
            skSolve(sketch);
        }
        {
            var Q0;
            Q0 = qSketchRegion(id + "F20", true);
            extrude(context, id + "F21", {"entities" : qUnion([Q0]), "depth" : 1 * mm, "offsetDistance" : 25 * mm});
        }
        {
            var Q0;
            Q0=makeQuery(id+"F21.opExtrude","SWEPT_BODY",BODY,{"disambiguationData":[OSD([sQuery(id+"F20.wireOp",EDGE,"E37"),sQuery(id+"F20.wireOp",EDGE,"E38.0")])]});
            var Q1;
            Q1=makeQuery(id+"F1.opExtrude","SWEPT_BODY",BODY,{"disambiguationData":[OSD([sQuery(id+"F0.wireOp",EDGE,"E0")])]});
            booleanBodies(context, id + "F22", {"operationType" : BooleanOperationType.SUBTRACTION, "tools" : qUnion([Q0]), "targets" : qUnion([Q1]), "keepTools" : true});
        }
        {
            var Q0;
            Q0=makeQuery(id+"F21.opExtrude","CAP_FACE",FACE,{"disambiguationData":[OSD([sQuery(id+"F20.wireOp",EDGE,"E37"),sQuery(id+"F20.wireOp",EDGE,"E38.0")])],"isStart":true});
            var sketch = newSketch(context, id + "F23", { "sketchPlane" : qUnion([Q0])});
            skCircle(sketch, "E39.0", {"center": v(-40, 0) * mm, "radius": 3 * mm});
            skCircle(sketch, "E40", {"center": v(-40, 0) * mm, "radius": 5 * mm});
            skSolve(sketch);
        }
        {
            var Q0;
            Q0 = qSketchRegion(id + "F23", true);
            extrude(context, id + "F24", {"entities" : qUnion([Q0]), "operationType" : NewBodyOperationType.ADD, "endBound" : BoundingType.UP_TO_NEXT, "depth" : 25 * mm, "offsetDistance" : 25 * mm});
        }
        {
            var Q0;
            Q0=makeQuery(id+"F21.opExtrude","CAP_FACE",FACE,{"disambiguationData":[OSD([sQuery(id+"F20.wireOp",EDGE,"E37"),sQuery(id+"F20.wireOp",EDGE,"E38.0")])],"isStart":false});
            var sketch = newSketch(context, id + "F25", { "sketchPlane" : qUnion([Q0])});
            skLineSegment(sketch, "E41.bottom", {"start": v(1.5, 71) * mm, "end": v(-1.5, 71) * mm});
            skLineSegment(sketch, "E41.top", {"start": v(1.5, 91) * mm, "end": v(-1.5, 91) * mm});
            skLineSegment(sketch, "E41.left", {"start": v(1.5, 71) * mm, "end": v(1.5, 91) * mm});
            skLineSegment(sketch, "E41.right", {"start": v(-1.5, 71) * mm, "end": v(-1.5, 91) * mm});
            skPoint(sketch, "E41.middle", {"position": v(0, 81) * mm});
            skLineSegment(sketch, "E42.1.0", {"start": v(-36.8, 60.74) * mm, "end": v(-46.8, 78.06) * mm});
            skLineSegment(sketch, "E42.1.1", {"start": v(-34.2, 62.24) * mm, "end": v(-44.2, 79.56) * mm});
            skLineSegment(sketch, "E42.1.2", {"start": v(-44.2, 79.56) * mm, "end": v(-46.8, 78.06) * mm});
            skLineSegment(sketch, "E42.1.3", {"start": v(-34.2, 62.24) * mm, "end": v(-36.8, 60.74) * mm});
            skLineSegment(sketch, "E42.2.0", {"start": v(-62.24, 34.2) * mm, "end": v(-79.56, 44.2) * mm});
            skLineSegment(sketch, "E42.2.1", {"start": v(-60.74, 36.8) * mm, "end": v(-78.06, 46.8) * mm});
            skLineSegment(sketch, "E42.2.2", {"start": v(-78.06, 46.8) * mm, "end": v(-79.56, 44.2) * mm});
            skLineSegment(sketch, "E42.2.3", {"start": v(-60.74, 36.8) * mm, "end": v(-62.24, 34.2) * mm});
            skLineSegment(sketch, "E42.3.0", {"start": v(-71, -1.5) * mm, "end": v(-91, -1.5) * mm});
            skLineSegment(sketch, "E42.3.1", {"start": v(-71, 1.5) * mm, "end": v(-91, 1.5) * mm});
            skLineSegment(sketch, "E42.3.2", {"start": v(-91, 1.5) * mm, "end": v(-91, -1.5) * mm});
            skLineSegment(sketch, "E42.3.3", {"start": v(-71, 1.5) * mm, "end": v(-71, -1.5) * mm});
            skLineSegment(sketch, "E42.4.0", {"start": v(-60.74, -36.8) * mm, "end": v(-78.06, -46.8) * mm});
            skLineSegment(sketch, "E42.4.1", {"start": v(-62.24, -34.2) * mm, "end": v(-79.56, -44.2) * mm});
            skLineSegment(sketch, "E42.4.2", {"start": v(-79.56, -44.2) * mm, "end": v(-78.06, -46.8) * mm});
            skLineSegment(sketch, "E42.4.3", {"start": v(-62.24, -34.2) * mm, "end": v(-60.74, -36.8) * mm});
            skLineSegment(sketch, "E42.5.0", {"start": v(-34.2, -62.24) * mm, "end": v(-44.2, -79.56) * mm});
            skLineSegment(sketch, "E42.5.1", {"start": v(-36.8, -60.74) * mm, "end": v(-46.8, -78.06) * mm});
            skLineSegment(sketch, "E42.5.2", {"start": v(-46.8, -78.06) * mm, "end": v(-44.2, -79.56) * mm});
            skLineSegment(sketch, "E42.5.3", {"start": v(-36.8, -60.74) * mm, "end": v(-34.2, -62.24) * mm});
            skLineSegment(sketch, "E42.6.0", {"start": v(1.5, -71) * mm, "end": v(1.5, -91) * mm});
            skLineSegment(sketch, "E42.6.1", {"start": v(-1.5, -71) * mm, "end": v(-1.5, -91) * mm});
            skLineSegment(sketch, "E42.6.2", {"start": v(-1.5, -91) * mm, "end": v(1.5, -91) * mm});
            skLineSegment(sketch, "E42.6.3", {"start": v(-1.5, -71) * mm, "end": v(1.5, -71) * mm});
            skLineSegment(sketch, "E42.7.0", {"start": v(36.8, -60.74) * mm, "end": v(46.8, -78.06) * mm});
            skLineSegment(sketch, "E42.7.1", {"start": v(34.2, -62.24) * mm, "end": v(44.2, -79.56) * mm});
            skLineSegment(sketch, "E42.7.2", {"start": v(44.2, -79.56) * mm, "end": v(46.8, -78.06) * mm});
            skLineSegment(sketch, "E42.7.3", {"start": v(34.2, -62.24) * mm, "end": v(36.8, -60.74) * mm});
            skLineSegment(sketch, "E42.8.0", {"start": v(62.24, -34.2) * mm, "end": v(79.56, -44.2) * mm});
            skLineSegment(sketch, "E42.8.1", {"start": v(60.74, -36.8) * mm, "end": v(78.06, -46.8) * mm});
            skLineSegment(sketch, "E42.8.2", {"start": v(78.06, -46.8) * mm, "end": v(79.56, -44.2) * mm});
            skLineSegment(sketch, "E42.8.3", {"start": v(60.74, -36.8) * mm, "end": v(62.24, -34.2) * mm});
            skLineSegment(sketch, "E42.9.0", {"start": v(71, 1.5) * mm, "end": v(91, 1.5) * mm});
            skLineSegment(sketch, "E42.9.1", {"start": v(71, -1.5) * mm, "end": v(91, -1.5) * mm});
            skLineSegment(sketch, "E42.9.2", {"start": v(91, -1.5) * mm, "end": v(91, 1.5) * mm});
            skLineSegment(sketch, "E42.9.3", {"start": v(71, -1.5) * mm, "end": v(71, 1.5) * mm});
            skLineSegment(sketch, "E42.10.0", {"start": v(60.74, 36.8) * mm, "end": v(78.06, 46.8) * mm});
            skLineSegment(sketch, "E42.10.1", {"start": v(62.24, 34.2) * mm, "end": v(79.56, 44.2) * mm});
            skLineSegment(sketch, "E42.10.2", {"start": v(79.56, 44.2) * mm, "end": v(78.06, 46.8) * mm});
            skLineSegment(sketch, "E42.10.3", {"start": v(62.24, 34.2) * mm, "end": v(60.74, 36.8) * mm});
            skLineSegment(sketch, "E42.11.0", {"start": v(34.2, 62.24) * mm, "end": v(44.2, 79.56) * mm});
            skLineSegment(sketch, "E42.11.1", {"start": v(36.8, 60.74) * mm, "end": v(46.8, 78.06) * mm});
            skLineSegment(sketch, "E42.11.2", {"start": v(46.8, 78.06) * mm, "end": v(44.2, 79.56) * mm});
            skLineSegment(sketch, "E42.11.3", {"start": v(36.8, 60.74) * mm, "end": v(34.2, 62.24) * mm});
            skPoint(sketch, "E42.center", {"position": v(0, 0) * mm});
            skSolve(sketch);
        }
        {
            var Q0;
            Q0 = qSketchRegion(id + "F25", true);
            extrude(context, id + "F26", {"entities" : qUnion([Q0]), "operationType" : NewBodyOperationType.REMOVE, "oppositeDirection" : true, "depth" : 0.5 * mm, "offsetDistance" : 25 * mm});
        }
        {
            var Q0;
            Q0=makeQuery(id+"F21.opExtrude","CAP_FACE",FACE,{"disambiguationData":[OSD([sQuery(id+"F20.wireOp",EDGE,"E37"),sQuery(id+"F20.wireOp",EDGE,"E38.0")])],"isStart":false});
            var sketch = newSketch(context, id + "F27", { "sketchPlane" : qUnion([Q0])});
            skLineSegment(sketch, "E43.bottom", {"start": v(-0.75, 90.5) * mm, "end": v(0.75, 90.5) * mm});
            skLineSegment(sketch, "E43.top", {"start": v(-0.75, 78.5) * mm, "end": v(0.75, 78.5) * mm});
            skLineSegment(sketch, "E43.left", {"start": v(-0.75, 90.5) * mm, "end": v(-0.75, 78.5) * mm});
            skLineSegment(sketch, "E43.right", {"start": v(0.75, 90.5) * mm, "end": v(0.75, 78.5) * mm});
            skPoint(sketch, "E43.middle", {"position": v(0, 84.5) * mm});
            skLineSegment(sketch, "E44.1.0", {"start": v(-10.2, 89.93) * mm, "end": v(-8.95, 78) * mm});
            skLineSegment(sketch, "E44.1.1", {"start": v(-10.2, 89.93) * mm, "end": v(-8.71, 90.08) * mm});
            skLineSegment(sketch, "E44.1.2", {"start": v(-8.71, 90.08) * mm, "end": v(-7.46, 78.15) * mm});
            skLineSegment(sketch, "E44.1.3", {"start": v(-8.95, 78) * mm, "end": v(-7.46, 78.15) * mm});
            skLineSegment(sketch, "E44.2.0", {"start": v(-19.55, 88.37) * mm, "end": v(-17.05, 76.63) * mm});
            skLineSegment(sketch, "E44.2.1", {"start": v(-19.55, 88.37) * mm, "end": v(-18.08, 88.68) * mm});
            skLineSegment(sketch, "E44.2.2", {"start": v(-18.08, 88.68) * mm, "end": v(-15.59, 76.94) * mm});
            skLineSegment(sketch, "E44.2.3", {"start": v(-17.05, 76.63) * mm, "end": v(-15.59, 76.94) * mm});
            skPoint(sketch, "E44.center", {"position": v(0, 0) * mm});
            skLineSegment(sketch, "E45.2.3.0", {"start": v(-28.68, 85.84) * mm, "end": v(-24.97, 74.43) * mm});
            skLineSegment(sketch, "E45.3.3.0", {"start": v(-28.68, 85.84) * mm, "end": v(-27.25, 86.3) * mm});
            skLineSegment(sketch, "E45.6.3.0", {"start": v(-27.25, 86.3) * mm, "end": v(-23.54, 74.89) * mm});
            skLineSegment(sketch, "E45.9.3.0", {"start": v(-24.97, 74.43) * mm, "end": v(-23.54, 74.89) * mm});
            skLineSegment(sketch, "E45.2.4.0", {"start": v(-37.5, 82.37) * mm, "end": v(-32.61, 71.4) * mm});
            skLineSegment(sketch, "E45.3.4.0", {"start": v(-37.5, 82.37) * mm, "end": v(-36.12, 82.98) * mm});
            skLineSegment(sketch, "E45.6.4.0", {"start": v(-36.12, 82.98) * mm, "end": v(-31.24, 72.02) * mm});
            skLineSegment(sketch, "E45.9.4.0", {"start": v(-32.61, 71.4) * mm, "end": v(-31.24, 72.02) * mm});
            skLineSegment(sketch, "E45.2.5.0", {"start": v(-45.9, 78) * mm, "end": v(-39.9, 67.6) * mm});
            skLineSegment(sketch, "E45.3.5.0", {"start": v(-45.9, 78) * mm, "end": v(-44.6, 78.75) * mm});
            skLineSegment(sketch, "E45.6.5.0", {"start": v(-44.6, 78.75) * mm, "end": v(-38.6, 68.36) * mm});
            skLineSegment(sketch, "E45.9.5.0", {"start": v(-39.9, 67.6) * mm, "end": v(-38.6, 68.36) * mm});
            skLineSegment(sketch, "E45.2.6.0", {"start": v(-53.8, 72.78) * mm, "end": v(-46.75, 63.07) * mm});
            skLineSegment(sketch, "E45.3.6.0", {"start": v(-53.8, 72.78) * mm, "end": v(-52.59, 73.66) * mm});
            skLineSegment(sketch, "E45.6.6.0", {"start": v(-52.59, 73.66) * mm, "end": v(-45.53, 63.95) * mm});
            skLineSegment(sketch, "E45.9.6.0", {"start": v(-46.75, 63.07) * mm, "end": v(-45.53, 63.95) * mm});
            skLineSegment(sketch, "E45.2.7.0", {"start": v(-61.11, 66.75) * mm, "end": v(-53.08, 57.84) * mm});
            skLineSegment(sketch, "E45.3.7.0", {"start": v(-61.11, 66.75) * mm, "end": v(-60, 67.76) * mm});
            skLineSegment(sketch, "E45.6.7.0", {"start": v(-60, 67.76) * mm, "end": v(-51.97, 58.84) * mm});
            skLineSegment(sketch, "E45.9.7.0", {"start": v(-53.08, 57.84) * mm, "end": v(-51.97, 58.84) * mm});
            skLineSegment(sketch, "E45.2.8.0", {"start": v(-67.76, 60) * mm, "end": v(-58.84, 51.97) * mm});
            skLineSegment(sketch, "E45.3.8.0", {"start": v(-67.76, 60) * mm, "end": v(-66.75, 61.11) * mm});
            skLineSegment(sketch, "E45.6.8.0", {"start": v(-66.75, 61.11) * mm, "end": v(-57.84, 53.08) * mm});
            skLineSegment(sketch, "E45.9.8.0", {"start": v(-58.84, 51.97) * mm, "end": v(-57.84, 53.08) * mm});
            skLineSegment(sketch, "E45.2.9.0", {"start": v(-73.66, 52.59) * mm, "end": v(-63.95, 45.53) * mm});
            skLineSegment(sketch, "E45.3.9.0", {"start": v(-73.66, 52.59) * mm, "end": v(-72.78, 53.8) * mm});
            skLineSegment(sketch, "E45.6.9.0", {"start": v(-72.78, 53.8) * mm, "end": v(-63.07, 46.75) * mm});
            skLineSegment(sketch, "E45.9.9.0", {"start": v(-63.95, 45.53) * mm, "end": v(-63.07, 46.75) * mm});
            skLineSegment(sketch, "E45.2.10.0", {"start": v(-78.75, 44.6) * mm, "end": v(-68.36, 38.6) * mm});
            skLineSegment(sketch, "E45.3.10.0", {"start": v(-78.75, 44.6) * mm, "end": v(-78, 45.9) * mm});
            skLineSegment(sketch, "E45.6.10.0", {"start": v(-78, 45.9) * mm, "end": v(-67.6, 39.9) * mm});
            skLineSegment(sketch, "E45.9.10.0", {"start": v(-68.36, 38.6) * mm, "end": v(-67.6, 39.9) * mm});
            skLineSegment(sketch, "E45.2.11.0", {"start": v(-82.98, 36.12) * mm, "end": v(-72.02, 31.24) * mm});
            skLineSegment(sketch, "E45.3.11.0", {"start": v(-82.98, 36.12) * mm, "end": v(-82.37, 37.5) * mm});
            skLineSegment(sketch, "E45.6.11.0", {"start": v(-82.37, 37.5) * mm, "end": v(-71.4, 32.61) * mm});
            skLineSegment(sketch, "E45.9.11.0", {"start": v(-72.02, 31.24) * mm, "end": v(-71.4, 32.61) * mm});
            skLineSegment(sketch, "E45.2.12.0", {"start": v(-86.3, 27.25) * mm, "end": v(-74.89, 23.54) * mm});
            skLineSegment(sketch, "E45.3.12.0", {"start": v(-86.3, 27.25) * mm, "end": v(-85.84, 28.68) * mm});
            skLineSegment(sketch, "E45.6.12.0", {"start": v(-85.84, 28.68) * mm, "end": v(-74.43, 24.97) * mm});
            skLineSegment(sketch, "E45.9.12.0", {"start": v(-74.89, 23.54) * mm, "end": v(-74.43, 24.97) * mm});
            skLineSegment(sketch, "E45.2.13.0", {"start": v(-88.68, 18.08) * mm, "end": v(-76.94, 15.59) * mm});
            skLineSegment(sketch, "E45.3.13.0", {"start": v(-88.68, 18.08) * mm, "end": v(-88.37, 19.55) * mm});
            skLineSegment(sketch, "E45.6.13.0", {"start": v(-88.37, 19.55) * mm, "end": v(-76.63, 17.05) * mm});
            skLineSegment(sketch, "E45.9.13.0", {"start": v(-76.94, 15.59) * mm, "end": v(-76.63, 17.05) * mm});
            skLineSegment(sketch, "E45.2.14.0", {"start": v(-90.08, 8.71) * mm, "end": v(-78.15, 7.46) * mm});
            skLineSegment(sketch, "E45.3.14.0", {"start": v(-90.08, 8.71) * mm, "end": v(-89.93, 10.2) * mm});
            skLineSegment(sketch, "E45.6.14.0", {"start": v(-89.93, 10.2) * mm, "end": v(-78, 8.95) * mm});
            skLineSegment(sketch, "E45.9.14.0", {"start": v(-78.15, 7.46) * mm, "end": v(-78, 8.95) * mm});
            skLineSegment(sketch, "E45.2.15.0", {"start": v(-90.5, -0.75) * mm, "end": v(-78.5, -0.75) * mm});
            skLineSegment(sketch, "E45.3.15.0", {"start": v(-90.5, -0.75) * mm, "end": v(-90.5, 0.75) * mm});
            skLineSegment(sketch, "E45.6.15.0", {"start": v(-90.5, 0.75) * mm, "end": v(-78.5, 0.75) * mm});
            skLineSegment(sketch, "E45.9.15.0", {"start": v(-78.5, -0.75) * mm, "end": v(-78.5, 0.75) * mm});
            skLineSegment(sketch, "E45.2.16.0", {"start": v(-89.93, -10.2) * mm, "end": v(-78, -8.95) * mm});
            skLineSegment(sketch, "E45.3.16.0", {"start": v(-89.93, -10.2) * mm, "end": v(-90.08, -8.71) * mm});
            skLineSegment(sketch, "E45.6.16.0", {"start": v(-90.08, -8.71) * mm, "end": v(-78.15, -7.46) * mm});
            skLineSegment(sketch, "E45.9.16.0", {"start": v(-78, -8.95) * mm, "end": v(-78.15, -7.46) * mm});
            skLineSegment(sketch, "E45.2.17.0", {"start": v(-88.37, -19.55) * mm, "end": v(-76.63, -17.05) * mm});
            skLineSegment(sketch, "E45.3.17.0", {"start": v(-88.37, -19.55) * mm, "end": v(-88.68, -18.08) * mm});
            skLineSegment(sketch, "E45.6.17.0", {"start": v(-88.68, -18.08) * mm, "end": v(-76.94, -15.59) * mm});
            skLineSegment(sketch, "E45.9.17.0", {"start": v(-76.63, -17.05) * mm, "end": v(-76.94, -15.59) * mm});
            skLineSegment(sketch, "E45.2.18.0", {"start": v(-85.84, -28.68) * mm, "end": v(-74.43, -24.97) * mm});
            skLineSegment(sketch, "E45.3.18.0", {"start": v(-85.84, -28.68) * mm, "end": v(-86.3, -27.25) * mm});
            skLineSegment(sketch, "E45.6.18.0", {"start": v(-86.3, -27.25) * mm, "end": v(-74.89, -23.54) * mm});
            skLineSegment(sketch, "E45.9.18.0", {"start": v(-74.43, -24.97) * mm, "end": v(-74.89, -23.54) * mm});
            skLineSegment(sketch, "E45.2.19.0", {"start": v(-82.37, -37.5) * mm, "end": v(-71.4, -32.61) * mm});
            skLineSegment(sketch, "E45.3.19.0", {"start": v(-82.37, -37.5) * mm, "end": v(-82.98, -36.12) * mm});
            skLineSegment(sketch, "E45.6.19.0", {"start": v(-82.98, -36.12) * mm, "end": v(-72.02, -31.24) * mm});
            skLineSegment(sketch, "E45.9.19.0", {"start": v(-71.4, -32.61) * mm, "end": v(-72.02, -31.24) * mm});
            skLineSegment(sketch, "E45.2.20.0", {"start": v(-78, -45.9) * mm, "end": v(-67.6, -39.9) * mm});
            skLineSegment(sketch, "E45.3.20.0", {"start": v(-78, -45.9) * mm, "end": v(-78.75, -44.6) * mm});
            skLineSegment(sketch, "E45.6.20.0", {"start": v(-78.75, -44.6) * mm, "end": v(-68.36, -38.6) * mm});
            skLineSegment(sketch, "E45.9.20.0", {"start": v(-67.6, -39.9) * mm, "end": v(-68.36, -38.6) * mm});
            skLineSegment(sketch, "E45.2.21.0", {"start": v(-72.78, -53.8) * mm, "end": v(-63.07, -46.75) * mm});
            skLineSegment(sketch, "E45.3.21.0", {"start": v(-72.78, -53.8) * mm, "end": v(-73.66, -52.59) * mm});
            skLineSegment(sketch, "E45.6.21.0", {"start": v(-73.66, -52.59) * mm, "end": v(-63.95, -45.53) * mm});
            skLineSegment(sketch, "E45.9.21.0", {"start": v(-63.07, -46.75) * mm, "end": v(-63.95, -45.53) * mm});
            skLineSegment(sketch, "E45.2.22.0", {"start": v(-66.75, -61.11) * mm, "end": v(-57.84, -53.08) * mm});
            skLineSegment(sketch, "E45.3.22.0", {"start": v(-66.75, -61.11) * mm, "end": v(-67.76, -60) * mm});
            skLineSegment(sketch, "E45.6.22.0", {"start": v(-67.76, -60) * mm, "end": v(-58.84, -51.97) * mm});
            skLineSegment(sketch, "E45.9.22.0", {"start": v(-57.84, -53.08) * mm, "end": v(-58.84, -51.97) * mm});
            skLineSegment(sketch, "E45.2.23.0", {"start": v(-60, -67.76) * mm, "end": v(-51.97, -58.84) * mm});
            skLineSegment(sketch, "E45.3.23.0", {"start": v(-60, -67.76) * mm, "end": v(-61.11, -66.75) * mm});
            skLineSegment(sketch, "E45.6.23.0", {"start": v(-61.11, -66.75) * mm, "end": v(-53.08, -57.84) * mm});
            skLineSegment(sketch, "E45.9.23.0", {"start": v(-51.97, -58.84) * mm, "end": v(-53.08, -57.84) * mm});
            skLineSegment(sketch, "E45.2.24.0", {"start": v(-52.59, -73.66) * mm, "end": v(-45.53, -63.95) * mm});
            skLineSegment(sketch, "E45.3.24.0", {"start": v(-52.59, -73.66) * mm, "end": v(-53.8, -72.78) * mm});
            skLineSegment(sketch, "E45.6.24.0", {"start": v(-53.8, -72.78) * mm, "end": v(-46.75, -63.07) * mm});
            skLineSegment(sketch, "E45.9.24.0", {"start": v(-45.53, -63.95) * mm, "end": v(-46.75, -63.07) * mm});
            skLineSegment(sketch, "E45.2.25.0", {"start": v(-44.6, -78.75) * mm, "end": v(-38.6, -68.36) * mm});
            skLineSegment(sketch, "E45.3.25.0", {"start": v(-44.6, -78.75) * mm, "end": v(-45.9, -78) * mm});
            skLineSegment(sketch, "E45.6.25.0", {"start": v(-45.9, -78) * mm, "end": v(-39.9, -67.6) * mm});
            skLineSegment(sketch, "E45.9.25.0", {"start": v(-38.6, -68.36) * mm, "end": v(-39.9, -67.6) * mm});
            skLineSegment(sketch, "E45.2.26.0", {"start": v(-36.12, -82.98) * mm, "end": v(-31.24, -72.02) * mm});
            skLineSegment(sketch, "E45.3.26.0", {"start": v(-36.12, -82.98) * mm, "end": v(-37.5, -82.37) * mm});
            skLineSegment(sketch, "E45.6.26.0", {"start": v(-37.5, -82.37) * mm, "end": v(-32.61, -71.4) * mm});
            skLineSegment(sketch, "E45.9.26.0", {"start": v(-31.24, -72.02) * mm, "end": v(-32.61, -71.4) * mm});
            skLineSegment(sketch, "E45.2.27.0", {"start": v(-27.25, -86.3) * mm, "end": v(-23.54, -74.89) * mm});
            skLineSegment(sketch, "E45.3.27.0", {"start": v(-27.25, -86.3) * mm, "end": v(-28.68, -85.84) * mm});
            skLineSegment(sketch, "E45.6.27.0", {"start": v(-28.68, -85.84) * mm, "end": v(-24.97, -74.43) * mm});
            skLineSegment(sketch, "E45.9.27.0", {"start": v(-23.54, -74.89) * mm, "end": v(-24.97, -74.43) * mm});
            skLineSegment(sketch, "E45.2.28.0", {"start": v(-18.08, -88.68) * mm, "end": v(-15.59, -76.94) * mm});
            skLineSegment(sketch, "E45.3.28.0", {"start": v(-18.08, -88.68) * mm, "end": v(-19.55, -88.37) * mm});
            skLineSegment(sketch, "E45.6.28.0", {"start": v(-19.55, -88.37) * mm, "end": v(-17.05, -76.63) * mm});
            skLineSegment(sketch, "E45.9.28.0", {"start": v(-15.59, -76.94) * mm, "end": v(-17.05, -76.63) * mm});
            skLineSegment(sketch, "E45.2.29.0", {"start": v(-8.71, -90.08) * mm, "end": v(-7.46, -78.15) * mm});
            skLineSegment(sketch, "E45.3.29.0", {"start": v(-8.71, -90.08) * mm, "end": v(-10.2, -89.93) * mm});
            skLineSegment(sketch, "E45.6.29.0", {"start": v(-10.2, -89.93) * mm, "end": v(-8.95, -78) * mm});
            skLineSegment(sketch, "E45.9.29.0", {"start": v(-7.46, -78.15) * mm, "end": v(-8.95, -78) * mm});
            skLineSegment(sketch, "E45.2.30.0", {"start": v(0.75, -90.5) * mm, "end": v(0.75, -78.5) * mm});
            skLineSegment(sketch, "E45.3.30.0", {"start": v(0.75, -90.5) * mm, "end": v(-0.75, -90.5) * mm});
            skLineSegment(sketch, "E45.6.30.0", {"start": v(-0.75, -90.5) * mm, "end": v(-0.75, -78.5) * mm});
            skLineSegment(sketch, "E45.9.30.0", {"start": v(0.75, -78.5) * mm, "end": v(-0.75, -78.5) * mm});
            skLineSegment(sketch, "E45.2.31.0", {"start": v(10.2, -89.93) * mm, "end": v(8.95, -78) * mm});
            skLineSegment(sketch, "E45.3.31.0", {"start": v(10.2, -89.93) * mm, "end": v(8.71, -90.08) * mm});
            skLineSegment(sketch, "E45.6.31.0", {"start": v(8.71, -90.08) * mm, "end": v(7.46, -78.15) * mm});
            skLineSegment(sketch, "E45.9.31.0", {"start": v(8.95, -78) * mm, "end": v(7.46, -78.15) * mm});
            skLineSegment(sketch, "E45.2.32.0", {"start": v(19.55, -88.37) * mm, "end": v(17.05, -76.63) * mm});
            skLineSegment(sketch, "E45.3.32.0", {"start": v(19.55, -88.37) * mm, "end": v(18.08, -88.68) * mm});
            skLineSegment(sketch, "E45.6.32.0", {"start": v(18.08, -88.68) * mm, "end": v(15.59, -76.94) * mm});
            skLineSegment(sketch, "E45.9.32.0", {"start": v(17.05, -76.63) * mm, "end": v(15.59, -76.94) * mm});
            skLineSegment(sketch, "E45.2.33.0", {"start": v(28.68, -85.84) * mm, "end": v(24.97, -74.43) * mm});
            skLineSegment(sketch, "E45.3.33.0", {"start": v(28.68, -85.84) * mm, "end": v(27.25, -86.3) * mm});
            skLineSegment(sketch, "E45.6.33.0", {"start": v(27.25, -86.3) * mm, "end": v(23.54, -74.89) * mm});
            skLineSegment(sketch, "E45.9.33.0", {"start": v(24.97, -74.43) * mm, "end": v(23.54, -74.89) * mm});
            skLineSegment(sketch, "E45.2.34.0", {"start": v(37.5, -82.37) * mm, "end": v(32.61, -71.4) * mm});
            skLineSegment(sketch, "E45.3.34.0", {"start": v(37.5, -82.37) * mm, "end": v(36.12, -82.98) * mm});
            skLineSegment(sketch, "E45.6.34.0", {"start": v(36.12, -82.98) * mm, "end": v(31.24, -72.02) * mm});
            skLineSegment(sketch, "E45.9.34.0", {"start": v(32.61, -71.4) * mm, "end": v(31.24, -72.02) * mm});
            skLineSegment(sketch, "E45.2.35.0", {"start": v(45.9, -78) * mm, "end": v(39.9, -67.6) * mm});
            skLineSegment(sketch, "E45.3.35.0", {"start": v(45.9, -78) * mm, "end": v(44.6, -78.75) * mm});
            skLineSegment(sketch, "E45.6.35.0", {"start": v(44.6, -78.75) * mm, "end": v(38.6, -68.36) * mm});
            skLineSegment(sketch, "E45.9.35.0", {"start": v(39.9, -67.6) * mm, "end": v(38.6, -68.36) * mm});
            skLineSegment(sketch, "E45.2.36.0", {"start": v(53.8, -72.78) * mm, "end": v(46.75, -63.07) * mm});
            skLineSegment(sketch, "E45.3.36.0", {"start": v(53.8, -72.78) * mm, "end": v(52.59, -73.66) * mm});
            skLineSegment(sketch, "E45.6.36.0", {"start": v(52.59, -73.66) * mm, "end": v(45.53, -63.95) * mm});
            skLineSegment(sketch, "E45.9.36.0", {"start": v(46.75, -63.07) * mm, "end": v(45.53, -63.95) * mm});
            skLineSegment(sketch, "E45.2.37.0", {"start": v(61.11, -66.75) * mm, "end": v(53.08, -57.84) * mm});
            skLineSegment(sketch, "E45.3.37.0", {"start": v(61.11, -66.75) * mm, "end": v(60, -67.76) * mm});
            skLineSegment(sketch, "E45.6.37.0", {"start": v(60, -67.76) * mm, "end": v(51.97, -58.84) * mm});
            skLineSegment(sketch, "E45.9.37.0", {"start": v(53.08, -57.84) * mm, "end": v(51.97, -58.84) * mm});
            skLineSegment(sketch, "E45.2.38.0", {"start": v(67.76, -60) * mm, "end": v(58.84, -51.97) * mm});
            skLineSegment(sketch, "E45.3.38.0", {"start": v(67.76, -60) * mm, "end": v(66.75, -61.11) * mm});
            skLineSegment(sketch, "E45.6.38.0", {"start": v(66.75, -61.11) * mm, "end": v(57.84, -53.08) * mm});
            skLineSegment(sketch, "E45.9.38.0", {"start": v(58.84, -51.97) * mm, "end": v(57.84, -53.08) * mm});
            skLineSegment(sketch, "E45.2.39.0", {"start": v(73.66, -52.59) * mm, "end": v(63.95, -45.53) * mm});
            skLineSegment(sketch, "E45.3.39.0", {"start": v(73.66, -52.59) * mm, "end": v(72.78, -53.8) * mm});
            skLineSegment(sketch, "E45.6.39.0", {"start": v(72.78, -53.8) * mm, "end": v(63.07, -46.75) * mm});
            skLineSegment(sketch, "E45.9.39.0", {"start": v(63.95, -45.53) * mm, "end": v(63.07, -46.75) * mm});
            skLineSegment(sketch, "E45.2.40.0", {"start": v(78.75, -44.6) * mm, "end": v(68.36, -38.6) * mm});
            skLineSegment(sketch, "E45.3.40.0", {"start": v(78.75, -44.6) * mm, "end": v(78, -45.9) * mm});
            skLineSegment(sketch, "E45.6.40.0", {"start": v(78, -45.9) * mm, "end": v(67.6, -39.9) * mm});
            skLineSegment(sketch, "E45.9.40.0", {"start": v(68.36, -38.6) * mm, "end": v(67.6, -39.9) * mm});
            skLineSegment(sketch, "E45.2.41.0", {"start": v(82.98, -36.12) * mm, "end": v(72.02, -31.24) * mm});
            skLineSegment(sketch, "E45.3.41.0", {"start": v(82.98, -36.12) * mm, "end": v(82.37, -37.5) * mm});
            skLineSegment(sketch, "E45.6.41.0", {"start": v(82.37, -37.5) * mm, "end": v(71.4, -32.61) * mm});
            skLineSegment(sketch, "E45.9.41.0", {"start": v(72.02, -31.24) * mm, "end": v(71.4, -32.61) * mm});
            skLineSegment(sketch, "E45.2.42.0", {"start": v(86.3, -27.25) * mm, "end": v(74.89, -23.54) * mm});
            skLineSegment(sketch, "E45.3.42.0", {"start": v(86.3, -27.25) * mm, "end": v(85.84, -28.68) * mm});
            skLineSegment(sketch, "E45.6.42.0", {"start": v(85.84, -28.68) * mm, "end": v(74.43, -24.97) * mm});
            skLineSegment(sketch, "E45.9.42.0", {"start": v(74.89, -23.54) * mm, "end": v(74.43, -24.97) * mm});
            skLineSegment(sketch, "E45.2.43.0", {"start": v(88.68, -18.08) * mm, "end": v(76.94, -15.59) * mm});
            skLineSegment(sketch, "E45.3.43.0", {"start": v(88.68, -18.08) * mm, "end": v(88.37, -19.55) * mm});
            skLineSegment(sketch, "E45.6.43.0", {"start": v(88.37, -19.55) * mm, "end": v(76.63, -17.05) * mm});
            skLineSegment(sketch, "E45.9.43.0", {"start": v(76.94, -15.59) * mm, "end": v(76.63, -17.05) * mm});
            skLineSegment(sketch, "E45.2.44.0", {"start": v(90.08, -8.71) * mm, "end": v(78.15, -7.46) * mm});
            skLineSegment(sketch, "E45.3.44.0", {"start": v(90.08, -8.71) * mm, "end": v(89.93, -10.2) * mm});
            skLineSegment(sketch, "E45.6.44.0", {"start": v(89.93, -10.2) * mm, "end": v(78, -8.95) * mm});
            skLineSegment(sketch, "E45.9.44.0", {"start": v(78.15, -7.46) * mm, "end": v(78, -8.95) * mm});
            skLineSegment(sketch, "E45.2.45.0", {"start": v(90.5, 0.75) * mm, "end": v(78.5, 0.75) * mm});
            skLineSegment(sketch, "E45.3.45.0", {"start": v(90.5, 0.75) * mm, "end": v(90.5, -0.75) * mm});
            skLineSegment(sketch, "E45.6.45.0", {"start": v(90.5, -0.75) * mm, "end": v(78.5, -0.75) * mm});
            skLineSegment(sketch, "E45.9.45.0", {"start": v(78.5, 0.75) * mm, "end": v(78.5, -0.75) * mm});
            skLineSegment(sketch, "E45.2.46.0", {"start": v(89.93, 10.2) * mm, "end": v(78, 8.95) * mm});
            skLineSegment(sketch, "E45.3.46.0", {"start": v(89.93, 10.2) * mm, "end": v(90.08, 8.71) * mm});
            skLineSegment(sketch, "E45.6.46.0", {"start": v(90.08, 8.71) * mm, "end": v(78.15, 7.46) * mm});
            skLineSegment(sketch, "E45.9.46.0", {"start": v(78, 8.95) * mm, "end": v(78.15, 7.46) * mm});
            skLineSegment(sketch, "E45.2.47.0", {"start": v(88.37, 19.55) * mm, "end": v(76.63, 17.05) * mm});
            skLineSegment(sketch, "E45.3.47.0", {"start": v(88.37, 19.55) * mm, "end": v(88.68, 18.08) * mm});
            skLineSegment(sketch, "E45.6.47.0", {"start": v(88.68, 18.08) * mm, "end": v(76.94, 15.59) * mm});
            skLineSegment(sketch, "E45.9.47.0", {"start": v(76.63, 17.05) * mm, "end": v(76.94, 15.59) * mm});
            skLineSegment(sketch, "E45.2.48.0", {"start": v(85.84, 28.68) * mm, "end": v(74.43, 24.97) * mm});
            skLineSegment(sketch, "E45.3.48.0", {"start": v(85.84, 28.68) * mm, "end": v(86.3, 27.25) * mm});
            skLineSegment(sketch, "E45.6.48.0", {"start": v(86.3, 27.25) * mm, "end": v(74.89, 23.54) * mm});
            skLineSegment(sketch, "E45.9.48.0", {"start": v(74.43, 24.97) * mm, "end": v(74.89, 23.54) * mm});
            skLineSegment(sketch, "E45.2.49.0", {"start": v(82.37, 37.5) * mm, "end": v(71.4, 32.61) * mm});
            skLineSegment(sketch, "E45.3.49.0", {"start": v(82.37, 37.5) * mm, "end": v(82.98, 36.12) * mm});
            skLineSegment(sketch, "E45.6.49.0", {"start": v(82.98, 36.12) * mm, "end": v(72.02, 31.24) * mm});
            skLineSegment(sketch, "E45.9.49.0", {"start": v(71.4, 32.61) * mm, "end": v(72.02, 31.24) * mm});
            skLineSegment(sketch, "E45.2.50.0", {"start": v(78, 45.9) * mm, "end": v(67.6, 39.9) * mm});
            skLineSegment(sketch, "E45.3.50.0", {"start": v(78, 45.9) * mm, "end": v(78.75, 44.6) * mm});
            skLineSegment(sketch, "E45.6.50.0", {"start": v(78.75, 44.6) * mm, "end": v(68.36, 38.6) * mm});
            skLineSegment(sketch, "E45.9.50.0", {"start": v(67.6, 39.9) * mm, "end": v(68.36, 38.6) * mm});
            skLineSegment(sketch, "E45.2.51.0", {"start": v(72.78, 53.8) * mm, "end": v(63.07, 46.75) * mm});
            skLineSegment(sketch, "E45.3.51.0", {"start": v(72.78, 53.8) * mm, "end": v(73.66, 52.59) * mm});
            skLineSegment(sketch, "E45.6.51.0", {"start": v(73.66, 52.59) * mm, "end": v(63.95, 45.53) * mm});
            skLineSegment(sketch, "E45.9.51.0", {"start": v(63.07, 46.75) * mm, "end": v(63.95, 45.53) * mm});
            skLineSegment(sketch, "E45.2.52.0", {"start": v(66.75, 61.11) * mm, "end": v(57.84, 53.08) * mm});
            skLineSegment(sketch, "E45.3.52.0", {"start": v(66.75, 61.11) * mm, "end": v(67.76, 60) * mm});
            skLineSegment(sketch, "E45.6.52.0", {"start": v(67.76, 60) * mm, "end": v(58.84, 51.97) * mm});
            skLineSegment(sketch, "E45.9.52.0", {"start": v(57.84, 53.08) * mm, "end": v(58.84, 51.97) * mm});
            skLineSegment(sketch, "E45.2.53.0", {"start": v(60, 67.76) * mm, "end": v(51.97, 58.84) * mm});
            skLineSegment(sketch, "E45.3.53.0", {"start": v(60, 67.76) * mm, "end": v(61.11, 66.75) * mm});
            skLineSegment(sketch, "E45.6.53.0", {"start": v(61.11, 66.75) * mm, "end": v(53.08, 57.84) * mm});
            skLineSegment(sketch, "E45.9.53.0", {"start": v(51.97, 58.84) * mm, "end": v(53.08, 57.84) * mm});
            skLineSegment(sketch, "E45.2.54.0", {"start": v(52.59, 73.66) * mm, "end": v(45.53, 63.95) * mm});
            skLineSegment(sketch, "E45.3.54.0", {"start": v(52.59, 73.66) * mm, "end": v(53.8, 72.78) * mm});
            skLineSegment(sketch, "E45.6.54.0", {"start": v(53.8, 72.78) * mm, "end": v(46.75, 63.07) * mm});
            skLineSegment(sketch, "E45.9.54.0", {"start": v(45.53, 63.95) * mm, "end": v(46.75, 63.07) * mm});
            skLineSegment(sketch, "E45.2.55.0", {"start": v(44.6, 78.75) * mm, "end": v(38.6, 68.36) * mm});
            skLineSegment(sketch, "E45.3.55.0", {"start": v(44.6, 78.75) * mm, "end": v(45.9, 78) * mm});
            skLineSegment(sketch, "E45.6.55.0", {"start": v(45.9, 78) * mm, "end": v(39.9, 67.6) * mm});
            skLineSegment(sketch, "E45.9.55.0", {"start": v(38.6, 68.36) * mm, "end": v(39.9, 67.6) * mm});
            skLineSegment(sketch, "E45.2.56.0", {"start": v(36.12, 82.98) * mm, "end": v(31.24, 72.02) * mm});
            skLineSegment(sketch, "E45.3.56.0", {"start": v(36.12, 82.98) * mm, "end": v(37.5, 82.37) * mm});
            skLineSegment(sketch, "E45.6.56.0", {"start": v(37.5, 82.37) * mm, "end": v(32.61, 71.4) * mm});
            skLineSegment(sketch, "E45.9.56.0", {"start": v(31.24, 72.02) * mm, "end": v(32.61, 71.4) * mm});
            skLineSegment(sketch, "E45.2.57.0", {"start": v(27.25, 86.3) * mm, "end": v(23.54, 74.89) * mm});
            skLineSegment(sketch, "E45.3.57.0", {"start": v(27.25, 86.3) * mm, "end": v(28.68, 85.84) * mm});
            skLineSegment(sketch, "E45.6.57.0", {"start": v(28.68, 85.84) * mm, "end": v(24.97, 74.43) * mm});
            skLineSegment(sketch, "E45.9.57.0", {"start": v(23.54, 74.89) * mm, "end": v(24.97, 74.43) * mm});
            skLineSegment(sketch, "E45.2.58.0", {"start": v(18.08, 88.68) * mm, "end": v(15.59, 76.94) * mm});
            skLineSegment(sketch, "E45.3.58.0", {"start": v(18.08, 88.68) * mm, "end": v(19.55, 88.37) * mm});
            skLineSegment(sketch, "E45.6.58.0", {"start": v(19.55, 88.37) * mm, "end": v(17.05, 76.63) * mm});
            skLineSegment(sketch, "E45.9.58.0", {"start": v(15.59, 76.94) * mm, "end": v(17.05, 76.63) * mm});
            skLineSegment(sketch, "E45.2.59.0", {"start": v(8.71, 90.08) * mm, "end": v(7.46, 78.15) * mm});
            skLineSegment(sketch, "E45.3.59.0", {"start": v(8.71, 90.08) * mm, "end": v(10.2, 89.93) * mm});
            skLineSegment(sketch, "E45.6.59.0", {"start": v(10.2, 89.93) * mm, "end": v(8.95, 78) * mm});
            skLineSegment(sketch, "E45.9.59.0", {"start": v(7.46, 78.15) * mm, "end": v(8.95, 78) * mm});
            skSolve(sketch);
        }
        {
            var Q0;
            Q0 = qSketchRegion(id + "F27", true);
            extrude(context, id + "F28", {"entities" : qUnion([Q0]), "operationType" : NewBodyOperationType.REMOVE, "oppositeDirection" : true, "depth" : 0.2 * mm, "offsetDistance" : 25 * mm});
        }
        {
            var Q0;
            Q0=makeQuery(id+"F26.boolean.opBoolean","COPY",FACE,{"derivedFrom":makeQuery(id+"F26.opExtrude","CAP_FACE",FACE,{"disambiguationData":[OSD([sQuery(id+"F25.wireOp",EDGE,"E41.bottom"),sQuery(id+"F25.wireOp",EDGE,"E41.top"),sQuery(id+"F25.wireOp",EDGE,"E41.left"),sQuery(id+"F25.wireOp",EDGE,"E41.right")])],"isStart":false})});
            extrude(context, id + "F29", {"entities" : qUnion([Q0]), "depth" : 1 * mm, "offsetDistance" : 25 * mm});
        }
        {
            var Q0;
            Q0=makeQuery(id+"F28.boolean.opBoolean","COPY",FACE,{"derivedFrom":makeQuery(id+"F28.opExtrude","CAP_FACE",FACE,{"disambiguationData":[OSD([sQuery(id+"F27.wireOp",EDGE,"E45.2.59.0"),sQuery(id+"F27.wireOp",EDGE,"E45.3.59.0"),sQuery(id+"F27.wireOp",EDGE,"E45.6.59.0"),sQuery(id+"F27.wireOp",EDGE,"E45.9.59.0")])],"isStart":false})});
            extrude(context, id + "F30", {"entities" : qUnion([Q0]), "depth" : 0.4 * mm, "offsetDistance" : 25 * mm});
        }
        {
            var Q0;
            Q0=makeQuery(id+"F15.opExtrude","CAP_FACE",FACE,{"disambiguationData":[OSD([sQuery(id+"F14.wireOp",EDGE,"E21.0"),sQuery(id+"F14.wireOp",EDGE,"E22"),sQuery(id+"F14.wireOp",EDGE,"E23"),sQuery(id+"F14.wireOp",EDGE,"E24"),sQuery(id+"F14.wireOp",EDGE,"E25.MirrorCS"),sQuery(id+"F14.wireOp",EDGE,"E26.MirrorCS"),sQuery(id+"F14.wireOp",EDGE,"E27.1.0"),sQuery(id+"F14.wireOp",EDGE,"E27.1.1"),sQuery(id+"F14.wireOp",EDGE,"E27.1.2"),sQuery(id+"F14.wireOp",EDGE,"E27.1.3"),sQuery(id+"F14.wireOp",EDGE,"E27.2.0"),sQuery(id+"F14.wireOp",EDGE,"E27.2.1"),sQuery(id+"F14.wireOp",EDGE,"E27.2.2"),sQuery(id+"F14.wireOp",EDGE,"E27.2.3"),sQuery(id+"F14.wireOp",EDGE,"E28.1.3.0"),sQuery(id+"F14.wireOp",EDGE,"E28.3.3.0"),sQuery(id+"F14.wireOp",EDGE,"E28.6.3.0"),sQuery(id+"F14.wireOp",EDGE,"E28.9.3.0"),sQuery(id+"F14.wireOp",EDGE,"E28.1.4.0"),sQuery(id+"F14.wireOp",EDGE,"E28.3.4.0"),sQuery(id+"F14.wireOp",EDGE,"E28.6.4.0"),sQuery(id+"F14.wireOp",EDGE,"E28.9.4.0"),sQuery(id+"F14.wireOp",EDGE,"E28.1.5.0"),sQuery(id+"F14.wireOp",EDGE,"E28.3.5.0"),sQuery(id+"F14.wireOp",EDGE,"E28.6.5.0"),sQuery(id+"F14.wireOp",EDGE,"E28.9.5.0"),sQuery(id+"F14.wireOp",EDGE,"E28.1.6.0"),sQuery(id+"F14.wireOp",EDGE,"E28.3.6.0"),sQuery(id+"F14.wireOp",EDGE,"E28.6.6.0"),sQuery(id+"F14.wireOp",EDGE,"E28.9.6.0"),sQuery(id+"F14.wireOp",EDGE,"E28.1.7.0"),sQuery(id+"F14.wireOp",EDGE,"E28.3.7.0"),sQuery(id+"F14.wireOp",EDGE,"E28.6.7.0"),sQuery(id+"F14.wireOp",EDGE,"E28.9.7.0"),sQuery(id+"F14.wireOp",EDGE,"E28.1.8.0"),sQuery(id+"F14.wireOp",EDGE,"E28.3.8.0"),sQuery(id+"F14.wireOp",EDGE,"E28.6.8.0"),sQuery(id+"F14.wireOp",EDGE,"E28.9.8.0"),sQuery(id+"F14.wireOp",EDGE,"E28.1.9.0"),sQuery(id+"F14.wireOp",EDGE,"E28.3.9.0"),sQuery(id+"F14.wireOp",EDGE,"E28.6.9.0"),sQuery(id+"F14.wireOp",EDGE,"E28.9.9.0"),sQuery(id+"F14.wireOp",EDGE,"E28.1.10.0"),sQuery(id+"F14.wireOp",EDGE,"E28.3.10.0"),sQuery(id+"F14.wireOp",EDGE,"E28.6.10.0"),sQuery(id+"F14.wireOp",EDGE,"E28.9.10.0"),sQuery(id+"F14.wireOp",EDGE,"E28.1.11.0"),sQuery(id+"F14.wireOp",EDGE,"E28.3.11.0"),sQuery(id+"F14.wireOp",EDGE,"E28.6.11.0"),sQuery(id+"F14.wireOp",EDGE,"E28.9.11.0"),sQuery(id+"F14.wireOp",EDGE,"E28.1.12.0"),sQuery(id+"F14.wireOp",EDGE,"E28.3.12.0"),sQuery(id+"F14.wireOp",EDGE,"E28.6.12.0"),sQuery(id+"F14.wireOp",EDGE,"E28.9.12.0"),sQuery(id+"F14.wireOp",EDGE,"E28.1.13.0"),sQuery(id+"F14.wireOp",EDGE,"E28.3.13.0"),sQuery(id+"F14.wireOp",EDGE,"E28.6.13.0"),sQuery(id+"F14.wireOp",EDGE,"E28.9.13.0"),sQuery(id+"F14.wireOp",EDGE,"E28.1.14.0"),sQuery(id+"F14.wireOp",EDGE,"E28.3.14.0"),sQuery(id+"F14.wireOp",EDGE,"E28.6.14.0"),sQuery(id+"F14.wireOp",EDGE,"E28.9.14.0"),sQuery(id+"F14.wireOp",EDGE,"E28.1.15.0"),sQuery(id+"F14.wireOp",EDGE,"E28.3.15.0"),sQuery(id+"F14.wireOp",EDGE,"E28.6.15.0"),sQuery(id+"F14.wireOp",EDGE,"E28.9.15.0"),sQuery(id+"F14.wireOp",EDGE,"E28.1.16.0"),sQuery(id+"F14.wireOp",EDGE,"E28.3.16.0"),sQuery(id+"F14.wireOp",EDGE,"E28.6.16.0"),sQuery(id+"F14.wireOp",EDGE,"E28.9.16.0"),sQuery(id+"F14.wireOp",EDGE,"E28.1.17.0"),sQuery(id+"F14.wireOp",EDGE,"E28.3.17.0"),sQuery(id+"F14.wireOp",EDGE,"E28.6.17.0"),sQuery(id+"F14.wireOp",EDGE,"E28.9.17.0"),sQuery(id+"F14.wireOp",EDGE,"E28.1.18.0"),sQuery(id+"F14.wireOp",EDGE,"E28.3.18.0"),sQuery(id+"F14.wireOp",EDGE,"E28.6.18.0"),sQuery(id+"F14.wireOp",EDGE,"E28.9.18.0"),sQuery(id+"F14.wireOp",EDGE,"E28.1.19.0"),sQuery(id+"F14.wireOp",EDGE,"E28.3.19.0"),sQuery(id+"F14.wireOp",EDGE,"E28.6.19.0"),sQuery(id+"F14.wireOp",EDGE,"E28.9.19.0"),sQuery(id+"F14.wireOp",EDGE,"E28.1.20.0"),sQuery(id+"F14.wireOp",EDGE,"E28.3.20.0"),sQuery(id+"F14.wireOp",EDGE,"E28.6.20.0"),sQuery(id+"F14.wireOp",EDGE,"E28.9.20.0"),sQuery(id+"F14.wireOp",EDGE,"E28.1.21.0"),sQuery(id+"F14.wireOp",EDGE,"E28.3.21.0"),sQuery(id+"F14.wireOp",EDGE,"E28.6.21.0"),sQuery(id+"F14.wireOp",EDGE,"E28.9.21.0"),sQuery(id+"F14.wireOp",EDGE,"E28.1.22.0"),sQuery(id+"F14.wireOp",EDGE,"E28.3.22.0"),sQuery(id+"F14.wireOp",EDGE,"E28.6.22.0"),sQuery(id+"F14.wireOp",EDGE,"E28.9.22.0"),sQuery(id+"F14.wireOp",EDGE,"E28.1.23.0"),sQuery(id+"F14.wireOp",EDGE,"E28.3.23.0"),sQuery(id+"F14.wireOp",EDGE,"E28.6.23.0"),sQuery(id+"F14.wireOp",EDGE,"E28.9.23.0"),sQuery(id+"F14.wireOp",EDGE,"E28.1.24.0"),sQuery(id+"F14.wireOp",EDGE,"E28.3.24.0"),sQuery(id+"F14.wireOp",EDGE,"E28.6.24.0"),sQuery(id+"F14.wireOp",EDGE,"E28.9.24.0"),sQuery(id+"F14.wireOp",EDGE,"E28.1.25.0"),sQuery(id+"F14.wireOp",EDGE,"E28.3.25.0"),sQuery(id+"F14.wireOp",EDGE,"E28.6.25.0"),sQuery(id+"F14.wireOp",EDGE,"E28.9.25.0"),sQuery(id+"F14.wireOp",EDGE,"E28.1.26.0"),sQuery(id+"F14.wireOp",EDGE,"E28.3.26.0"),sQuery(id+"F14.wireOp",EDGE,"E28.6.26.0"),sQuery(id+"F14.wireOp",EDGE,"E28.9.26.0"),sQuery(id+"F14.wireOp",EDGE,"E28.1.27.0"),sQuery(id+"F14.wireOp",EDGE,"E28.3.27.0"),sQuery(id+"F14.wireOp",EDGE,"E28.6.27.0"),sQuery(id+"F14.wireOp",EDGE,"E28.9.27.0"),sQuery(id+"F14.wireOp",EDGE,"E28.1.28.0"),sQuery(id+"F14.wireOp",EDGE,"E28.3.28.0"),sQuery(id+"F14.wireOp",EDGE,"E28.6.28.0"),sQuery(id+"F14.wireOp",EDGE,"E28.9.28.0"),sQuery(id+"F14.wireOp",EDGE,"E28.1.29.0"),sQuery(id+"F14.wireOp",EDGE,"E28.3.29.0"),sQuery(id+"F14.wireOp",EDGE,"E28.6.29.0"),sQuery(id+"F14.wireOp",EDGE,"E28.9.29.0"),sQuery(id+"F14.wireOp",EDGE,"E28.1.30.0"),sQuery(id+"F14.wireOp",EDGE,"E28.3.30.0"),sQuery(id+"F14.wireOp",EDGE,"E28.6.30.0"),sQuery(id+"F14.wireOp",EDGE,"E28.9.30.0"),sQuery(id+"F14.wireOp",EDGE,"E28.1.31.0"),sQuery(id+"F14.wireOp",EDGE,"E28.3.31.0"),sQuery(id+"F14.wireOp",EDGE,"E28.6.31.0"),sQuery(id+"F14.wireOp",EDGE,"E28.9.31.0"),sQuery(id+"F14.wireOp",EDGE,"E28.1.32.0"),sQuery(id+"F14.wireOp",EDGE,"E28.3.32.0"),sQuery(id+"F14.wireOp",EDGE,"E28.6.32.0"),sQuery(id+"F14.wireOp",EDGE,"E28.9.32.0"),sQuery(id+"F14.wireOp",EDGE,"E28.1.33.0"),sQuery(id+"F14.wireOp",EDGE,"E28.3.33.0"),sQuery(id+"F14.wireOp",EDGE,"E28.6.33.0"),sQuery(id+"F14.wireOp",EDGE,"E28.9.33.0"),sQuery(id+"F14.wireOp",EDGE,"E28.1.34.0"),sQuery(id+"F14.wireOp",EDGE,"E28.3.34.0"),sQuery(id+"F14.wireOp",EDGE,"E28.6.34.0"),sQuery(id+"F14.wireOp",EDGE,"E28.9.34.0"),sQuery(id+"F14.wireOp",EDGE,"E28.1.35.0"),sQuery(id+"F14.wireOp",EDGE,"E28.3.35.0"),sQuery(id+"F14.wireOp",EDGE,"E28.6.35.0"),sQuery(id+"F14.wireOp",EDGE,"E28.9.35.0"),sQuery(id+"F14.wireOp",EDGE,"E28.1.36.0"),sQuery(id+"F14.wireOp",EDGE,"E28.3.36.0"),sQuery(id+"F14.wireOp",EDGE,"E28.6.36.0"),sQuery(id+"F14.wireOp",EDGE,"E28.9.36.0"),sQuery(id+"F14.wireOp",EDGE,"E28.1.37.0"),sQuery(id+"F14.wireOp",EDGE,"E28.3.37.0"),sQuery(id+"F14.wireOp",EDGE,"E28.6.37.0"),sQuery(id+"F14.wireOp",EDGE,"E28.9.37.0"),sQuery(id+"F14.wireOp",EDGE,"E28.1.38.0"),sQuery(id+"F14.wireOp",EDGE,"E28.3.38.0"),sQuery(id+"F14.wireOp",EDGE,"E28.6.38.0"),sQuery(id+"F14.wireOp",EDGE,"E28.9.38.0"),sQuery(id+"F14.wireOp",EDGE,"E28.1.39.0"),sQuery(id+"F14.wireOp",EDGE,"E28.3.39.0"),sQuery(id+"F14.wireOp",EDGE,"E28.6.39.0"),sQuery(id+"F14.wireOp",EDGE,"E28.9.39.0")])],"isStart":false});
            var sketch = newSketch(context, id + "F31", { "sketchPlane" : qUnion([Q0])});
            skCircle(sketch, "E46.0", {"center": v(0, 0) * mm, "radius": 3 * mm});
            skCircle(sketch, "E47.0", {"center": v(0, 0) * mm, "radius": 5 * mm});
            skSolve(sketch);
        }
        {
            var Q0;
            Q0 = qSketchRegion(id + "F31", true);
            extrude(context, id + "F32", {"entities" : qUnion([Q0]), "operationType" : NewBodyOperationType.ADD, "depth" : 5 * mm, "offsetDistance" : 25 * mm});
        }
        {
            var Q0;
            Q0=makeQuery(id+"F32.opExtrude","CAP_FACE",FACE,{"disambiguationData":[OSD([sQuery(id+"F31.wireOp",EDGE,"E46.0"),sQuery(id+"F31.wireOp",EDGE,"E47.0")])],"isStart":false});
            var sketch = newSketch(context, id + "F33", { "sketchPlane" : qUnion([Q0])});
            skCircle(sketch, "E48.0", {"center": v(0, 0) * mm, "radius": 5 * mm});
            skCircle(sketch, "E49.0", {"center": v(0, 0) * mm, "radius": 3 * mm});
            skLineSegment(sketch, "E50", {"start": v(0, 50) * mm, "end": v(1.5, 50) * mm});
            skLineSegment(sketch, "E51", {"start": v(1.5, 50) * mm, "end": v(3, 4) * mm});
            skLineSegment(sketch, "E52.MirrorCS", {"start": v(0, 50) * mm, "end": v(-1.5, 50) * mm});
            skLineSegment(sketch, "E53.MirrorCS", {"start": v(-1.5, 50) * mm, "end": v(-3, 4) * mm});
            skSolve(sketch);
        }
        {
            var Q0;
            Q0 = qSketchRegion(id + "F33", true);
            extrude(context, id + "F34", {"entities" : qUnion([Q0]), "operationType" : NewBodyOperationType.ADD, "depth" : 1 * mm, "offsetDistance" : 25 * mm});
        }
        {
            var Q0;
            Q0=makeQuery(id+"F6.opExtrude","CAP_FACE",FACE,{"disambiguationData":[OSD([sQuery(id+"F0.wireOp",EDGE,"E0")])],"isStart":false});
            var sketch = newSketch(context, id + "F35", { "sketchPlane" : qUnion([Q0])});
            skCircle(sketch, "E54", {"center": v(0, 0) * mm, "radius": 5 * mm});
            skLineSegment(sketch, "E55", {"start": v(0, 85) * mm, "end": v(0.5, 85) * mm});
            skLineSegment(sketch, "E56", {"start": v(0.5, 85) * mm, "end": v(2, 4.58) * mm});
            skLineSegment(sketch, "E57.MirrorCS", {"start": v(0, 85) * mm, "end": v(-0.5, 85) * mm});
            skLineSegment(sketch, "E58.MirrorCS", {"start": v(-0.5, 85) * mm, "end": v(-2, 4.58) * mm});
            skSolve(sketch);
        }
        {
            var Q0;
            Q0 = qSketchRegion(id + "F35", true);
            extrude(context, id + "F36", {"entities" : qUnion([Q0]), "operationType" : NewBodyOperationType.ADD, "oppositeDirection" : true, "depth" : 1 * mm, "offsetDistance" : 25 * mm});
        }
    });
